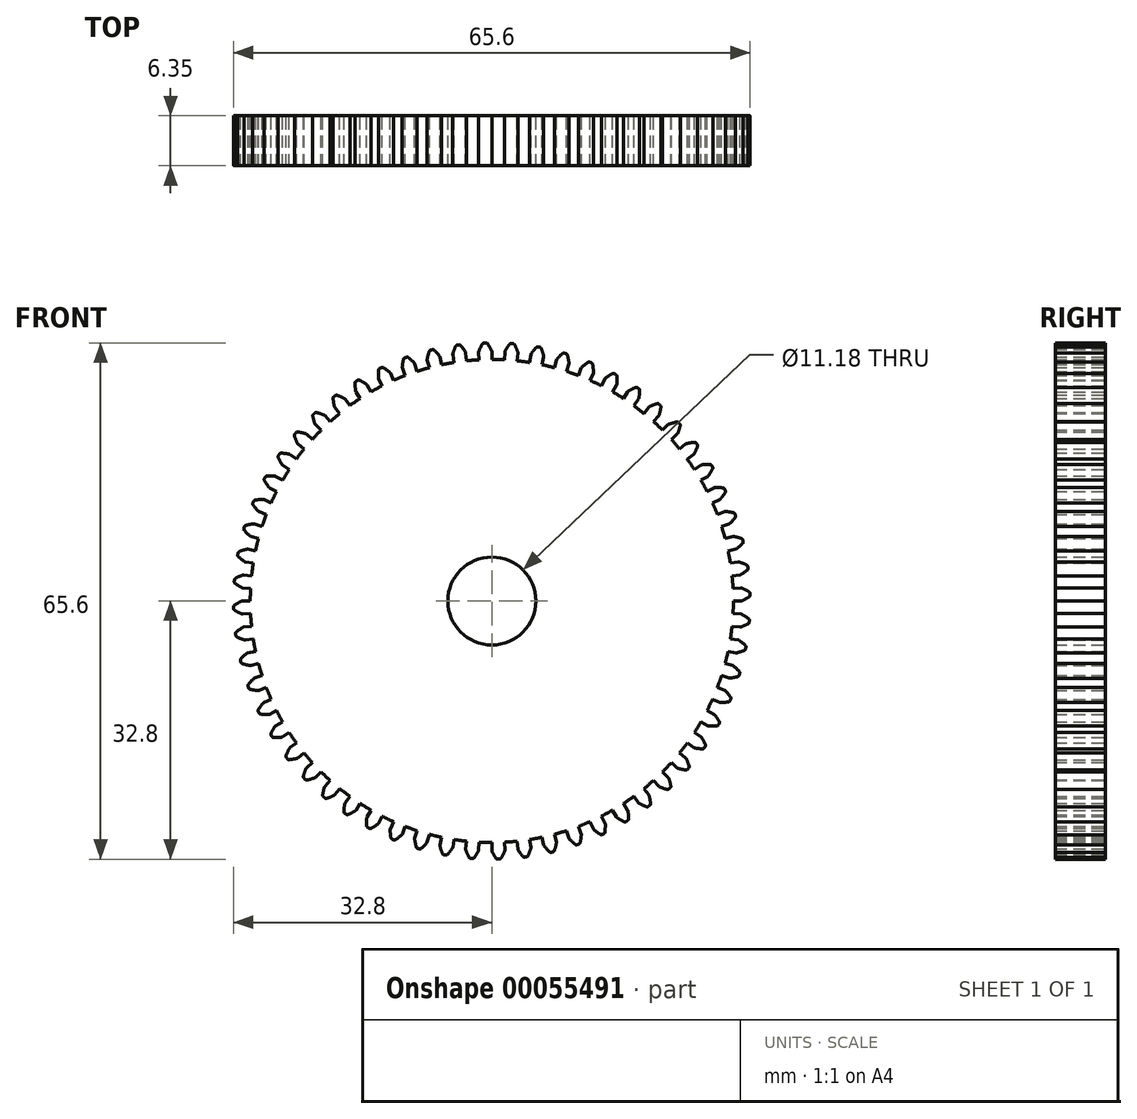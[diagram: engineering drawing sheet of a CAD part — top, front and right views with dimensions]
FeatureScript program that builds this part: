
annotation { "Feature Type Name" : "Feature", "Feature Type Description" : "" }
export const myFeature = defineFeature(function(context is Context, id is Id, definition is map)
    precondition{}
    {
        {
            var Q0;
            Q0=qCreatedBy(makeId("Front.planeOp"),FACE);
            var sketch = newSketch(context, id + "F0", { "sketchPlane" : qUnion([Q0])});
            skCircle(sketch, "E0", {"center": v(0, 0) * mm, "radius": 30.68 * mm});
            skLineSegment(sketch, "E1", {"start": v(0, 0) * mm, "end": v(-0.62, 23.84) * mm, "construction": true});
            skArc(sketch, "E2.trimOffspring", {"start": v(-0.03, 31.8) * mm, "mid": v(-0.26, 32.25) * mm, "end": v(-0.52, 32.68) * mm});
            skLineSegment(sketch, "E3.trimOffspring", {"start": v(-0.62, 23.84) * mm, "end": v(-0.62, 23.84) * mm});
            skArc(sketch, "E4.trimOffspring", {"start": v(-0.74, 32.8) * mm, "mid": v(-0.8, 32.8) * mm, "end": v(-0.86, 32.8) * mm});
            skPoint(sketch, "E5.orphan", {"position": v(-2.53, 48.29) * mm});
            skLineSegment(sketch, "E6", {"start": v(0, 31.7) * mm, "end": v(0, 30.68) * mm});
            skArc(sketch, "E7.MirrorCS", {"start": v(-0.98, 32.79) * mm, "mid": v(-0.92, 32.8) * mm, "end": v(-0.86, 32.8) * mm});
            skArc(sketch, "E8.MirrorCS", {"start": v(-1.64, 31.76) * mm, "mid": v(-1.43, 32.22) * mm, "end": v(-1.19, 32.66) * mm});
            skLineSegment(sketch, "E9.MirrorCS", {"start": v(-1.66, 31.65) * mm, "end": v(-1.6, 30.64) * mm});
            skPoint(sketch, "E10.orphan", {"position": v(-1.26, 48.29) * mm});
            skPoint(sketch, "E11.visualSharp", {"position": v(-1.66, 31.7) * mm});
            skArc(sketch, "E11.filletArc", {"start": v(-1.64, 31.76) * mm, "mid": v(-1.66, 31.7) * mm, "end": v(-1.66, 31.65) * mm});
            skPoint(sketch, "E12.visualSharp", {"position": v(-0.6, 32.8) * mm});
            skArc(sketch, "E12.filletArc", {"start": v(-0.52, 32.68) * mm, "mid": v(-0.62, 32.77) * mm, "end": v(-0.74, 32.8) * mm});
            skPoint(sketch, "E13.visualSharp", {"position": v(-1.12, 32.79) * mm});
            skArc(sketch, "E13.filletArc", {"start": v(-0.98, 32.79) * mm, "mid": v(-1.1, 32.75) * mm, "end": v(-1.19, 32.66) * mm});
            skArc(sketch, "E14.filletArc", {"start": v(0, 31.7) * mm, "mid": v(0, 31.75) * mm, "end": v(-0.03, 31.8) * mm});
            skArc(sketch, "E15.1.0", {"start": v(-4.95, 31.42) * mm, "mid": v(-4.79, 31.9) * mm, "end": v(-4.6, 32.36) * mm});
            skLineSegment(sketch, "E15.1.1", {"start": v(-3.31, 31.52) * mm, "end": v(-3.2, 30.52) * mm});
            skLineSegment(sketch, "E15.1.2", {"start": v(-4.96, 31.3) * mm, "end": v(-4.8, 30.3) * mm});
            skPoint(sketch, "E15.1.3", {"position": v(-4.03, 32.56) * mm});
            skPoint(sketch, "E15.1.4", {"position": v(-3.32, 31.58) * mm});
            skArc(sketch, "E15.1.5", {"start": v(-3.35, 31.63) * mm, "mid": v(-3.63, 32.05) * mm, "end": v(-3.94, 32.45) * mm});
            skPoint(sketch, "E15.1.6", {"position": v(-4.54, 32.49) * mm});
            skPoint(sketch, "E15.1.7", {"position": v(-4.97, 31.36) * mm});
            skArc(sketch, "E15.1.8", {"start": v(-3.94, 32.45) * mm, "mid": v(-4.04, 32.52) * mm, "end": v(-4.17, 32.54) * mm});
            skArc(sketch, "E15.1.9", {"start": v(-4.4, 32.5) * mm, "mid": v(-4.52, 32.46) * mm, "end": v(-4.6, 32.36) * mm});
            skArc(sketch, "E15.1.10", {"start": v(-4.4, 32.5) * mm, "mid": v(-4.34, 32.52) * mm, "end": v(-4.28, 32.52) * mm});
            skArc(sketch, "E15.1.11", {"start": v(-4.17, 32.54) * mm, "mid": v(-4.22, 32.53) * mm, "end": v(-4.28, 32.52) * mm});
            skArc(sketch, "E15.1.12", {"start": v(-4.95, 31.42) * mm, "mid": v(-4.96, 31.36) * mm, "end": v(-4.96, 31.3) * mm});
            skArc(sketch, "E15.1.13", {"start": v(-3.31, 31.52) * mm, "mid": v(-3.33, 31.57) * mm, "end": v(-3.35, 31.63) * mm});
            skArc(sketch, "E15.2.0", {"start": v(-8.2, 30.73) * mm, "mid": v(-8.1, 31.22) * mm, "end": v(-7.95, 31.7) * mm});
            skLineSegment(sketch, "E15.2.1", {"start": v(-6.59, 31) * mm, "end": v(-6.38, 30.01) * mm});
            skLineSegment(sketch, "E15.2.2", {"start": v(-8.2, 30.61) * mm, "end": v(-7.94, 29.64) * mm});
            skPoint(sketch, "E15.2.3", {"position": v(-7.4, 31.96) * mm});
            skPoint(sketch, "E15.2.4", {"position": v(-6.6, 31.06) * mm});
            skArc(sketch, "E15.2.5", {"start": v(-6.64, 31.1) * mm, "mid": v(-6.96, 31.5) * mm, "end": v(-7.3, 31.86) * mm});
            skPoint(sketch, "E15.2.6", {"position": v(-7.9, 31.84) * mm});
            skPoint(sketch, "E15.2.7", {"position": v(-8.22, 30.67) * mm});
            skArc(sketch, "E15.2.8", {"start": v(-7.3, 31.86) * mm, "mid": v(-7.42, 31.92) * mm, "end": v(-7.54, 31.92) * mm});
            skArc(sketch, "E15.2.9", {"start": v(-7.77, 31.87) * mm, "mid": v(-7.88, 31.8) * mm, "end": v(-7.95, 31.7) * mm});
            skArc(sketch, "E15.2.10", {"start": v(-7.77, 31.87) * mm, "mid": v(-7.71, 31.88) * mm, "end": v(-7.66, 31.9) * mm});
            skArc(sketch, "E15.2.11", {"start": v(-7.54, 31.92) * mm, "mid": v(-7.6, 31.91) * mm, "end": v(-7.66, 31.9) * mm});
            skArc(sketch, "E15.2.12", {"start": v(-8.2, 30.73) * mm, "mid": v(-8.21, 30.67) * mm, "end": v(-8.2, 30.61) * mm});
            skArc(sketch, "E15.2.13", {"start": v(-6.59, 31) * mm, "mid": v(-6.6, 31.05) * mm, "end": v(-6.64, 31.1) * mm});
            skArc(sketch, "E15.3.0", {"start": v(-11.37, 29.7) * mm, "mid": v(-11.31, 30.2) * mm, "end": v(-11.22, 30.7) * mm});
            skLineSegment(sketch, "E15.3.1", {"start": v(-9.8, 30.14) * mm, "end": v(-9.48, 29.18) * mm});
            skLineSegment(sketch, "E15.3.2", {"start": v(-11.36, 29.59) * mm, "end": v(-11, 28.65) * mm});
            skPoint(sketch, "E15.3.3", {"position": v(-10.7, 31) * mm});
            skPoint(sketch, "E15.3.4", {"position": v(-9.81, 30.2) * mm});
            skArc(sketch, "E15.3.5", {"start": v(-9.85, 30.24) * mm, "mid": v(-10.21, 30.6) * mm, "end": v(-10.6, 30.92) * mm});
            skPoint(sketch, "E15.3.6", {"position": v(-11.2, 30.84) * mm});
            skPoint(sketch, "E15.3.7", {"position": v(-11.38, 29.64) * mm});
            skArc(sketch, "E15.3.8", {"start": v(-10.6, 30.92) * mm, "mid": v(-10.71, 30.97) * mm, "end": v(-10.84, 30.96) * mm});
            skArc(sketch, "E15.3.9", {"start": v(-11.06, 30.88) * mm, "mid": v(-11.17, 30.81) * mm, "end": v(-11.22, 30.7) * mm});
            skArc(sketch, "E15.3.10", {"start": v(-11.06, 30.88) * mm, "mid": v(-11, 30.9) * mm, "end": v(-10.95, 30.92) * mm});
            skArc(sketch, "E15.3.11", {"start": v(-10.84, 30.96) * mm, "mid": v(-10.9, 30.94) * mm, "end": v(-10.95, 30.92) * mm});
            skArc(sketch, "E15.3.12", {"start": v(-11.37, 29.7) * mm, "mid": v(-11.37, 29.64) * mm, "end": v(-11.36, 29.59) * mm});
            skArc(sketch, "E15.3.13", {"start": v(-9.8, 30.14) * mm, "mid": v(-9.82, 30.2) * mm, "end": v(-9.85, 30.24) * mm});
            skArc(sketch, "E15.4.0", {"start": v(-14.42, 28.35) * mm, "mid": v(-14.4, 28.85) * mm, "end": v(-14.37, 29.36) * mm});
            skLineSegment(sketch, "E15.4.1", {"start": v(-12.9, 28.95) * mm, "end": v(-12.48, 28.03) * mm});
            skLineSegment(sketch, "E15.4.2", {"start": v(-14.39, 28.24) * mm, "end": v(-13.93, 27.34) * mm});
            skPoint(sketch, "E15.4.3", {"position": v(-13.9, 29.72) * mm});
            skPoint(sketch, "E15.4.4", {"position": v(-12.91, 29) * mm});
            skArc(sketch, "E15.4.5", {"start": v(-12.96, 29.04) * mm, "mid": v(-13.36, 29.36) * mm, "end": v(-13.77, 29.64) * mm});
            skPoint(sketch, "E15.4.6", {"position": v(-14.35, 29.5) * mm});
            skPoint(sketch, "E15.4.7", {"position": v(-14.41, 28.29) * mm});
            skArc(sketch, "E15.4.8", {"start": v(-13.77, 29.64) * mm, "mid": v(-13.9, 29.68) * mm, "end": v(-14.02, 29.66) * mm});
            skArc(sketch, "E15.4.9", {"start": v(-14.23, 29.56) * mm, "mid": v(-14.33, 29.48) * mm, "end": v(-14.37, 29.36) * mm});
            skArc(sketch, "E15.4.10", {"start": v(-14.23, 29.56) * mm, "mid": v(-14.18, 29.58) * mm, "end": v(-14.12, 29.6) * mm});
            skArc(sketch, "E15.4.11", {"start": v(-14.02, 29.66) * mm, "mid": v(-14.07, 29.63) * mm, "end": v(-14.12, 29.6) * mm});
            skArc(sketch, "E15.4.12", {"start": v(-14.42, 28.35) * mm, "mid": v(-14.4, 28.3) * mm, "end": v(-14.39, 28.24) * mm});
            skArc(sketch, "E15.4.13", {"start": v(-12.9, 28.95) * mm, "mid": v(-12.92, 29) * mm, "end": v(-12.96, 29.04) * mm});
            skArc(sketch, "E15.5.0", {"start": v(-17.3, 26.69) * mm, "mid": v(-17.35, 27.19) * mm, "end": v(-17.36, 27.7) * mm});
            skLineSegment(sketch, "E15.5.1", {"start": v(-15.85, 27.45) * mm, "end": v(-15.34, 26.57) * mm});
            skLineSegment(sketch, "E15.5.2", {"start": v(-17.26, 26.58) * mm, "end": v(-16.71, 25.73) * mm});
            skPoint(sketch, "E15.5.3", {"position": v(-16.92, 28.1) * mm});
            skPoint(sketch, "E15.5.4", {"position": v(-15.87, 27.5) * mm});
            skArc(sketch, "E15.5.5", {"start": v(-15.92, 27.53) * mm, "mid": v(-16.35, 27.8) * mm, "end": v(-16.8, 28.04) * mm});
            skPoint(sketch, "E15.5.6", {"position": v(-17.36, 27.84) * mm});
            skPoint(sketch, "E15.5.7", {"position": v(-17.3, 26.63) * mm});
            skArc(sketch, "E15.5.8", {"start": v(-16.8, 28.04) * mm, "mid": v(-16.92, 28.07) * mm, "end": v(-17.04, 28.03) * mm});
            skArc(sketch, "E15.5.9", {"start": v(-17.24, 27.9) * mm, "mid": v(-17.33, 27.82) * mm, "end": v(-17.36, 27.7) * mm});
            skArc(sketch, "E15.5.10", {"start": v(-17.24, 27.9) * mm, "mid": v(-17.19, 27.94) * mm, "end": v(-17.14, 27.97) * mm});
            skArc(sketch, "E15.5.11", {"start": v(-17.04, 28.03) * mm, "mid": v(-17.1, 28) * mm, "end": v(-17.14, 27.97) * mm});
            skArc(sketch, "E15.5.12", {"start": v(-17.3, 26.69) * mm, "mid": v(-17.29, 26.63) * mm, "end": v(-17.26, 26.58) * mm});
            skArc(sketch, "E15.5.13", {"start": v(-15.85, 27.45) * mm, "mid": v(-15.88, 27.5) * mm, "end": v(-15.92, 27.53) * mm});
            skArc(sketch, "E15.6.0", {"start": v(-20, 24.73) * mm, "mid": v(-20.1, 25.23) * mm, "end": v(-20.16, 25.73) * mm});
            skLineSegment(sketch, "E15.6.1", {"start": v(-18.63, 25.64) * mm, "end": v(-18.04, 24.82) * mm});
            skLineSegment(sketch, "E15.6.2", {"start": v(-19.94, 24.63) * mm, "end": v(-19.3, 23.85) * mm});
            skPoint(sketch, "E15.6.3", {"position": v(-19.77, 26.18) * mm});
            skPoint(sketch, "E15.6.4", {"position": v(-18.66, 25.69) * mm});
            skArc(sketch, "E15.6.5", {"start": v(-18.71, 25.71) * mm, "mid": v(-19.17, 25.94) * mm, "end": v(-19.63, 26.13) * mm});
            skPoint(sketch, "E15.6.6", {"position": v(-20.17, 25.87) * mm});
            skPoint(sketch, "E15.6.7", {"position": v(-19.98, 24.67) * mm});
            skArc(sketch, "E15.6.8", {"start": v(-19.63, 26.13) * mm, "mid": v(-19.76, 26.15) * mm, "end": v(-19.88, 26.1) * mm});
            skArc(sketch, "E15.6.9", {"start": v(-20.06, 25.95) * mm, "mid": v(-20.14, 25.85) * mm, "end": v(-20.16, 25.73) * mm});
            skArc(sketch, "E15.6.10", {"start": v(-20.06, 25.95) * mm, "mid": v(-20.02, 25.99) * mm, "end": v(-19.97, 26.03) * mm});
            skArc(sketch, "E15.6.11", {"start": v(-19.88, 26.1) * mm, "mid": v(-19.92, 26.06) * mm, "end": v(-19.97, 26.03) * mm});
            skArc(sketch, "E15.6.12", {"start": v(-20, 24.73) * mm, "mid": v(-19.98, 24.68) * mm, "end": v(-19.94, 24.63) * mm});
            skArc(sketch, "E15.6.13", {"start": v(-18.63, 25.64) * mm, "mid": v(-18.67, 25.68) * mm, "end": v(-18.71, 25.71) * mm});
            skArc(sketch, "E15.7.0", {"start": v(-22.47, 22.5) * mm, "mid": v(-22.62, 22.99) * mm, "end": v(-22.74, 23.48) * mm});
            skLineSegment(sketch, "E15.7.1", {"start": v(-21.2, 23.55) * mm, "end": v(-20.53, 22.8) * mm});
            skLineSegment(sketch, "E15.7.2", {"start": v(-22.4, 22.4) * mm, "end": v(-21.7, 21.7) * mm});
            skPoint(sketch, "E15.7.3", {"position": v(-22.4, 23.97) * mm});
            skPoint(sketch, "E15.7.4", {"position": v(-21.24, 23.6) * mm});
            skArc(sketch, "E15.7.5", {"start": v(-21.3, 23.62) * mm, "mid": v(-21.77, 23.8) * mm, "end": v(-22.26, 23.94) * mm});
            skPoint(sketch, "E15.7.6", {"position": v(-22.77, 23.62) * mm});
            skPoint(sketch, "E15.7.7", {"position": v(-22.45, 22.45) * mm});
            skArc(sketch, "E15.7.8", {"start": v(-22.26, 23.94) * mm, "mid": v(-22.38, 23.94) * mm, "end": v(-22.5, 23.88) * mm});
            skArc(sketch, "E15.7.9", {"start": v(-22.67, 23.71) * mm, "mid": v(-22.73, 23.6) * mm, "end": v(-22.74, 23.48) * mm});
            skArc(sketch, "E15.7.10", {"start": v(-22.67, 23.71) * mm, "mid": v(-22.62, 23.75) * mm, "end": v(-22.58, 23.8) * mm});
            skArc(sketch, "E15.7.11", {"start": v(-22.5, 23.88) * mm, "mid": v(-22.54, 23.84) * mm, "end": v(-22.58, 23.8) * mm});
            skArc(sketch, "E15.7.12", {"start": v(-22.47, 22.5) * mm, "mid": v(-22.45, 22.45) * mm, "end": v(-22.4, 22.4) * mm});
            skArc(sketch, "E15.7.13", {"start": v(-21.2, 23.55) * mm, "mid": v(-21.25, 23.59) * mm, "end": v(-21.3, 23.62) * mm});
            skArc(sketch, "E15.8.0", {"start": v(-24.7, 20.03) * mm, "mid": v(-24.9, 20.5) * mm, "end": v(-25.07, 20.97) * mm});
            skLineSegment(sketch, "E15.8.1", {"start": v(-23.55, 21.2) * mm, "end": v(-22.8, 20.53) * mm});
            skLineSegment(sketch, "E15.8.2", {"start": v(-24.63, 19.94) * mm, "end": v(-23.85, 19.3) * mm});
            skPoint(sketch, "E15.8.3", {"position": v(-24.78, 21.5) * mm});
            skPoint(sketch, "E15.8.4", {"position": v(-23.6, 21.24) * mm});
            skArc(sketch, "E15.8.5", {"start": v(-23.65, 21.26) * mm, "mid": v(-24.14, 21.39) * mm, "end": v(-24.64, 21.48) * mm});
            skPoint(sketch, "E15.8.6", {"position": v(-25.11, 21.1) * mm});
            skPoint(sketch, "E15.8.7", {"position": v(-24.67, 19.98) * mm});
            skArc(sketch, "E15.8.8", {"start": v(-24.64, 21.48) * mm, "mid": v(-24.76, 21.47) * mm, "end": v(-24.87, 21.4) * mm});
            skArc(sketch, "E15.8.9", {"start": v(-25.02, 21.22) * mm, "mid": v(-25.08, 21.1) * mm, "end": v(-25.07, 20.97) * mm});
            skArc(sketch, "E15.8.10", {"start": v(-25.02, 21.22) * mm, "mid": v(-24.98, 21.26) * mm, "end": v(-24.94, 21.3) * mm});
            skArc(sketch, "E15.8.11", {"start": v(-24.87, 21.4) * mm, "mid": v(-24.9, 21.35) * mm, "end": v(-24.94, 21.3) * mm});
            skArc(sketch, "E15.8.12", {"start": v(-24.7, 20.03) * mm, "mid": v(-24.67, 19.99) * mm, "end": v(-24.63, 19.94) * mm});
            skArc(sketch, "E15.8.13", {"start": v(-23.55, 21.2) * mm, "mid": v(-23.6, 21.24) * mm, "end": v(-23.65, 21.26) * mm});
            skArc(sketch, "E15.9.0", {"start": v(-26.66, 17.34) * mm, "mid": v(-26.9, 17.78) * mm, "end": v(-27.12, 18.24) * mm});
            skLineSegment(sketch, "E15.9.1", {"start": v(-25.64, 18.63) * mm, "end": v(-24.82, 18.04) * mm});
            skLineSegment(sketch, "E15.9.2", {"start": v(-26.58, 17.26) * mm, "end": v(-25.73, 16.71) * mm});
            skPoint(sketch, "E15.9.3", {"position": v(-26.89, 18.8) * mm});
            skPoint(sketch, "E15.9.4", {"position": v(-25.69, 18.66) * mm});
            skArc(sketch, "E15.9.5", {"start": v(-25.74, 18.67) * mm, "mid": v(-26.24, 18.75) * mm, "end": v(-26.75, 18.79) * mm});
            skPoint(sketch, "E15.9.6", {"position": v(-27.18, 18.37) * mm});
            skPoint(sketch, "E15.9.7", {"position": v(-26.63, 17.3) * mm});
            skArc(sketch, "E15.9.8", {"start": v(-26.75, 18.79) * mm, "mid": v(-26.87, 18.76) * mm, "end": v(-26.97, 18.68) * mm});
            skArc(sketch, "E15.9.9", {"start": v(-27.1, 18.48) * mm, "mid": v(-27.14, 18.36) * mm, "end": v(-27.12, 18.24) * mm});
            skArc(sketch, "E15.9.10", {"start": v(-27.1, 18.48) * mm, "mid": v(-27.07, 18.53) * mm, "end": v(-27.03, 18.58) * mm});
            skArc(sketch, "E15.9.11", {"start": v(-26.97, 18.68) * mm, "mid": v(-27, 18.63) * mm, "end": v(-27.03, 18.58) * mm});
            skArc(sketch, "E15.9.12", {"start": v(-26.66, 17.34) * mm, "mid": v(-26.62, 17.3) * mm, "end": v(-26.58, 17.26) * mm});
            skArc(sketch, "E15.9.13", {"start": v(-25.64, 18.63) * mm, "mid": v(-25.69, 18.66) * mm, "end": v(-25.74, 18.67) * mm});
            skArc(sketch, "E15.10.0", {"start": v(-28.33, 14.46) * mm, "mid": v(-28.62, 14.87) * mm, "end": v(-28.88, 15.3) * mm});
            skLineSegment(sketch, "E15.10.1", {"start": v(-27.45, 15.85) * mm, "end": v(-26.57, 15.34) * mm});
            skLineSegment(sketch, "E15.10.2", {"start": v(-28.24, 14.39) * mm, "end": v(-27.34, 13.93) * mm});
            skPoint(sketch, "E15.10.3", {"position": v(-28.7, 15.88) * mm});
            skPoint(sketch, "E15.10.4", {"position": v(-27.5, 15.88) * mm});
            skArc(sketch, "E15.10.5", {"start": v(-27.56, 15.88) * mm, "mid": v(-28.06, 15.9) * mm, "end": v(-28.56, 15.89) * mm});
            skPoint(sketch, "E15.10.6", {"position": v(-28.95, 15.43) * mm});
            skPoint(sketch, "E15.10.7", {"position": v(-28.29, 14.41) * mm});
            skArc(sketch, "E15.10.8", {"start": v(-28.56, 15.89) * mm, "mid": v(-28.69, 15.85) * mm, "end": v(-28.77, 15.76) * mm});
            skArc(sketch, "E15.10.9", {"start": v(-28.88, 15.55) * mm, "mid": v(-28.91, 15.43) * mm, "end": v(-28.88, 15.3) * mm});
            skArc(sketch, "E15.10.10", {"start": v(-28.88, 15.55) * mm, "mid": v(-28.86, 15.6) * mm, "end": v(-28.83, 15.65) * mm});
            skArc(sketch, "E15.10.11", {"start": v(-28.77, 15.76) * mm, "mid": v(-28.8, 15.7) * mm, "end": v(-28.83, 15.65) * mm});
            skArc(sketch, "E15.10.12", {"start": v(-28.33, 14.46) * mm, "mid": v(-28.29, 14.42) * mm, "end": v(-28.24, 14.39) * mm});
            skArc(sketch, "E15.10.13", {"start": v(-27.45, 15.85) * mm, "mid": v(-27.5, 15.87) * mm, "end": v(-27.56, 15.88) * mm});
            skArc(sketch, "E15.11.0", {"start": v(-29.68, 11.42) * mm, "mid": v(-30.01, 11.8) * mm, "end": v(-30.32, 12.2) * mm});
            skLineSegment(sketch, "E15.11.1", {"start": v(-28.95, 12.9) * mm, "end": v(-28.03, 12.48) * mm});
            skLineSegment(sketch, "E15.11.2", {"start": v(-29.59, 11.36) * mm, "end": v(-28.65, 11) * mm});
            skPoint(sketch, "E15.11.3", {"position": v(-30.2, 12.8) * mm});
            skPoint(sketch, "E15.11.4", {"position": v(-29, 12.91) * mm});
            skArc(sketch, "E15.11.5", {"start": v(-29.06, 12.91) * mm, "mid": v(-29.57, 12.88) * mm, "end": v(-30.07, 12.81) * mm});
            skPoint(sketch, "E15.11.6", {"position": v(-30.4, 12.32) * mm});
            skPoint(sketch, "E15.11.7", {"position": v(-29.64, 11.38) * mm});
            skArc(sketch, "E15.11.8", {"start": v(-30.07, 12.81) * mm, "mid": v(-30.18, 12.76) * mm, "end": v(-30.26, 12.66) * mm});
            skArc(sketch, "E15.11.9", {"start": v(-30.35, 12.45) * mm, "mid": v(-30.37, 12.32) * mm, "end": v(-30.32, 12.2) * mm});
            skArc(sketch, "E15.11.10", {"start": v(-30.35, 12.45) * mm, "mid": v(-30.33, 12.5) * mm, "end": v(-30.3, 12.55) * mm});
            skArc(sketch, "E15.11.11", {"start": v(-30.26, 12.66) * mm, "mid": v(-30.28, 12.6) * mm, "end": v(-30.3, 12.55) * mm});
            skArc(sketch, "E15.11.12", {"start": v(-29.68, 11.42) * mm, "mid": v(-29.64, 11.38) * mm, "end": v(-29.59, 11.36) * mm});
            skArc(sketch, "E15.11.13", {"start": v(-28.95, 12.9) * mm, "mid": v(-29, 12.9) * mm, "end": v(-29.06, 12.91) * mm});
            skArc(sketch, "E15.12.0", {"start": v(-30.71, 8.26) * mm, "mid": v(-31.08, 8.6) * mm, "end": v(-31.43, 8.96) * mm});
            skLineSegment(sketch, "E15.12.1", {"start": v(-30.14, 9.8) * mm, "end": v(-29.18, 9.48) * mm});
            skLineSegment(sketch, "E15.12.2", {"start": v(-30.61, 8.2) * mm, "end": v(-29.64, 7.94) * mm});
            skPoint(sketch, "E15.12.3", {"position": v(-31.38, 9.56) * mm});
            skPoint(sketch, "E15.12.4", {"position": v(-30.2, 9.81) * mm});
            skArc(sketch, "E15.12.5", {"start": v(-30.25, 9.8) * mm, "mid": v(-30.75, 9.72) * mm, "end": v(-31.24, 9.6) * mm});
            skPoint(sketch, "E15.12.6", {"position": v(-31.53, 9.07) * mm});
            skPoint(sketch, "E15.12.7", {"position": v(-30.67, 8.22) * mm});
            skArc(sketch, "E15.12.8", {"start": v(-31.24, 9.6) * mm, "mid": v(-31.35, 9.54) * mm, "end": v(-31.42, 9.43) * mm});
            skArc(sketch, "E15.12.9", {"start": v(-31.49, 9.2) * mm, "mid": v(-31.5, 9.08) * mm, "end": v(-31.43, 8.96) * mm});
            skArc(sketch, "E15.12.10", {"start": v(-31.49, 9.2) * mm, "mid": v(-31.47, 9.26) * mm, "end": v(-31.45, 9.32) * mm});
            skArc(sketch, "E15.12.11", {"start": v(-31.42, 9.43) * mm, "mid": v(-31.44, 9.37) * mm, "end": v(-31.45, 9.32) * mm});
            skArc(sketch, "E15.12.12", {"start": v(-30.71, 8.26) * mm, "mid": v(-30.67, 8.22) * mm, "end": v(-30.61, 8.2) * mm});
            skArc(sketch, "E15.12.13", {"start": v(-30.14, 9.8) * mm, "mid": v(-30.2, 9.8) * mm, "end": v(-30.25, 9.8) * mm});
            skArc(sketch, "E15.13.0", {"start": v(-31.4, 5) * mm, "mid": v(-31.81, 5.3) * mm, "end": v(-32.2, 5.63) * mm});
            skLineSegment(sketch, "E15.13.1", {"start": v(-31, 6.59) * mm, "end": v(-30.01, 6.38) * mm});
            skLineSegment(sketch, "E15.13.2", {"start": v(-31.3, 4.96) * mm, "end": v(-30.3, 4.8) * mm});
            skPoint(sketch, "E15.13.3", {"position": v(-32.2, 6.23) * mm});
            skPoint(sketch, "E15.13.4", {"position": v(-31.06, 6.6) * mm});
            skArc(sketch, "E15.13.5", {"start": v(-31.11, 6.59) * mm, "mid": v(-31.6, 6.45) * mm, "end": v(-32.08, 6.28) * mm});
            skPoint(sketch, "E15.13.6", {"position": v(-32.3, 5.73) * mm});
            skPoint(sketch, "E15.13.7", {"position": v(-31.36, 4.97) * mm});
            skArc(sketch, "E15.13.8", {"start": v(-32.08, 6.28) * mm, "mid": v(-32.18, 6.2) * mm, "end": v(-32.23, 6.1) * mm});
            skArc(sketch, "E15.13.9", {"start": v(-32.28, 5.86) * mm, "mid": v(-32.27, 5.74) * mm, "end": v(-32.2, 5.63) * mm});
            skArc(sketch, "E15.13.10", {"start": v(-32.28, 5.86) * mm, "mid": v(-32.27, 5.92) * mm, "end": v(-32.25, 5.98) * mm});
            skArc(sketch, "E15.13.11", {"start": v(-32.23, 6.1) * mm, "mid": v(-32.24, 6.04) * mm, "end": v(-32.25, 5.98) * mm});
            skArc(sketch, "E15.13.12", {"start": v(-31.4, 5) * mm, "mid": v(-31.36, 4.97) * mm, "end": v(-31.3, 4.96) * mm});
            skArc(sketch, "E15.13.13", {"start": v(-31, 6.59) * mm, "mid": v(-31.06, 6.6) * mm, "end": v(-31.11, 6.59) * mm});
            skArc(sketch, "E15.14.0", {"start": v(-31.76, 1.69) * mm, "mid": v(-32.2, 1.95) * mm, "end": v(-32.6, 2.23) * mm});
            skLineSegment(sketch, "E15.14.1", {"start": v(-31.52, 3.31) * mm, "end": v(-30.52, 3.2) * mm});
            skLineSegment(sketch, "E15.14.2", {"start": v(-31.65, 1.66) * mm, "end": v(-30.64, 1.6) * mm});
            skPoint(sketch, "E15.14.3", {"position": v(-32.68, 2.83) * mm});
            skPoint(sketch, "E15.14.4", {"position": v(-31.58, 3.32) * mm});
            skArc(sketch, "E15.14.5", {"start": v(-31.63, 3.3) * mm, "mid": v(-32.1, 3.11) * mm, "end": v(-32.56, 2.9) * mm});
            skPoint(sketch, "E15.14.6", {"position": v(-32.72, 2.32) * mm});
            skPoint(sketch, "E15.14.7", {"position": v(-31.7, 1.66) * mm});
            skArc(sketch, "E15.14.8", {"start": v(-32.56, 2.9) * mm, "mid": v(-32.65, 2.81) * mm, "end": v(-32.7, 2.7) * mm});
            skArc(sketch, "E15.14.9", {"start": v(-32.71, 2.46) * mm, "mid": v(-32.69, 2.33) * mm, "end": v(-32.6, 2.23) * mm});
            skArc(sketch, "E15.14.10", {"start": v(-32.71, 2.46) * mm, "mid": v(-32.7, 2.52) * mm, "end": v(-32.7, 2.57) * mm});
            skArc(sketch, "E15.14.11", {"start": v(-32.7, 2.7) * mm, "mid": v(-32.7, 2.63) * mm, "end": v(-32.7, 2.57) * mm});
            skArc(sketch, "E15.14.12", {"start": v(-31.76, 1.69) * mm, "mid": v(-31.7, 1.67) * mm, "end": v(-31.65, 1.66) * mm});
            skArc(sketch, "E15.14.13", {"start": v(-31.52, 3.31) * mm, "mid": v(-31.58, 3.31) * mm, "end": v(-31.63, 3.3) * mm});
            skArc(sketch, "E15.15.0", {"start": v(-31.76, -1.64) * mm, "mid": v(-32.22, -1.43) * mm, "end": v(-32.66, -1.19) * mm});
            skLineSegment(sketch, "E15.15.1", {"start": v(-31.7, 0) * mm, "end": v(-30.68, 0) * mm});
            skLineSegment(sketch, "E15.15.2", {"start": v(-31.65, -1.66) * mm, "end": v(-30.64, -1.6) * mm});
            skPoint(sketch, "E15.15.3", {"position": v(-32.8, -0.6) * mm});
            skPoint(sketch, "E15.15.4", {"position": v(-31.75, 0) * mm});
            skArc(sketch, "E15.15.5", {"start": v(-31.8, -0.03) * mm, "mid": v(-32.25, -0.26) * mm, "end": v(-32.68, -0.52) * mm});
            skPoint(sketch, "E15.15.6", {"position": v(-32.79, -1.12) * mm});
            skPoint(sketch, "E15.15.7", {"position": v(-31.7, -1.66) * mm});
            skArc(sketch, "E15.15.8", {"start": v(-32.68, -0.52) * mm, "mid": v(-32.77, -0.62) * mm, "end": v(-32.8, -0.74) * mm});
            skArc(sketch, "E15.15.9", {"start": v(-32.79, -0.98) * mm, "mid": v(-32.75, -1.1) * mm, "end": v(-32.66, -1.19) * mm});
            skArc(sketch, "E15.15.10", {"start": v(-32.79, -0.98) * mm, "mid": v(-32.8, -0.92) * mm, "end": v(-32.8, -0.86) * mm});
            skArc(sketch, "E15.15.11", {"start": v(-32.8, -0.74) * mm, "mid": v(-32.8, -0.8) * mm, "end": v(-32.8, -0.86) * mm});
            skArc(sketch, "E15.15.12", {"start": v(-31.76, -1.64) * mm, "mid": v(-31.7, -1.66) * mm, "end": v(-31.65, -1.66) * mm});
            skArc(sketch, "E15.15.13", {"start": v(-31.7, 0) * mm, "mid": v(-31.75, 0) * mm, "end": v(-31.8, -0.03) * mm});
            skArc(sketch, "E15.16.0", {"start": v(-31.42, -4.95) * mm, "mid": v(-31.9, -4.79) * mm, "end": v(-32.36, -4.6) * mm});
            skLineSegment(sketch, "E15.16.1", {"start": v(-31.52, -3.31) * mm, "end": v(-30.52, -3.2) * mm});
            skLineSegment(sketch, "E15.16.2", {"start": v(-31.3, -4.96) * mm, "end": v(-30.3, -4.8) * mm});
            skPoint(sketch, "E15.16.3", {"position": v(-32.56, -4.03) * mm});
            skPoint(sketch, "E15.16.4", {"position": v(-31.58, -3.32) * mm});
            skArc(sketch, "E15.16.5", {"start": v(-31.63, -3.35) * mm, "mid": v(-32.05, -3.63) * mm, "end": v(-32.45, -3.94) * mm});
            skPoint(sketch, "E15.16.6", {"position": v(-32.49, -4.54) * mm});
            skPoint(sketch, "E15.16.7", {"position": v(-31.36, -4.97) * mm});
            skArc(sketch, "E15.16.8", {"start": v(-32.45, -3.94) * mm, "mid": v(-32.52, -4.04) * mm, "end": v(-32.54, -4.17) * mm});
            skArc(sketch, "E15.16.9", {"start": v(-32.5, -4.4) * mm, "mid": v(-32.46, -4.52) * mm, "end": v(-32.36, -4.6) * mm});
            skArc(sketch, "E15.16.10", {"start": v(-32.5, -4.4) * mm, "mid": v(-32.52, -4.34) * mm, "end": v(-32.52, -4.28) * mm});
            skArc(sketch, "E15.16.11", {"start": v(-32.54, -4.17) * mm, "mid": v(-32.53, -4.22) * mm, "end": v(-32.52, -4.28) * mm});
            skArc(sketch, "E15.16.12", {"start": v(-31.42, -4.95) * mm, "mid": v(-31.36, -4.96) * mm, "end": v(-31.3, -4.96) * mm});
            skArc(sketch, "E15.16.13", {"start": v(-31.52, -3.31) * mm, "mid": v(-31.57, -3.33) * mm, "end": v(-31.63, -3.35) * mm});
            skArc(sketch, "E15.17.0", {"start": v(-30.73, -8.2) * mm, "mid": v(-31.22, -8.1) * mm, "end": v(-31.7, -7.95) * mm});
            skLineSegment(sketch, "E15.17.1", {"start": v(-31, -6.59) * mm, "end": v(-30.01, -6.38) * mm});
            skLineSegment(sketch, "E15.17.2", {"start": v(-30.61, -8.2) * mm, "end": v(-29.64, -7.94) * mm});
            skPoint(sketch, "E15.17.3", {"position": v(-31.96, -7.4) * mm});
            skPoint(sketch, "E15.17.4", {"position": v(-31.06, -6.6) * mm});
            skArc(sketch, "E15.17.5", {"start": v(-31.1, -6.64) * mm, "mid": v(-31.5, -6.96) * mm, "end": v(-31.86, -7.3) * mm});
            skPoint(sketch, "E15.17.6", {"position": v(-31.84, -7.9) * mm});
            skPoint(sketch, "E15.17.7", {"position": v(-30.67, -8.22) * mm});
            skArc(sketch, "E15.17.8", {"start": v(-31.86, -7.3) * mm, "mid": v(-31.92, -7.42) * mm, "end": v(-31.92, -7.54) * mm});
            skArc(sketch, "E15.17.9", {"start": v(-31.87, -7.77) * mm, "mid": v(-31.8, -7.88) * mm, "end": v(-31.7, -7.95) * mm});
            skArc(sketch, "E15.17.10", {"start": v(-31.87, -7.77) * mm, "mid": v(-31.88, -7.71) * mm, "end": v(-31.9, -7.66) * mm});
            skArc(sketch, "E15.17.11", {"start": v(-31.92, -7.54) * mm, "mid": v(-31.91, -7.6) * mm, "end": v(-31.9, -7.66) * mm});
            skArc(sketch, "E15.17.12", {"start": v(-30.73, -8.2) * mm, "mid": v(-30.67, -8.21) * mm, "end": v(-30.61, -8.2) * mm});
            skArc(sketch, "E15.17.13", {"start": v(-31, -6.59) * mm, "mid": v(-31.05, -6.6) * mm, "end": v(-31.1, -6.64) * mm});
            skArc(sketch, "E15.18.0", {"start": v(-29.7, -11.37) * mm, "mid": v(-30.2, -11.31) * mm, "end": v(-30.7, -11.22) * mm});
            skLineSegment(sketch, "E15.18.1", {"start": v(-30.14, -9.8) * mm, "end": v(-29.18, -9.48) * mm});
            skLineSegment(sketch, "E15.18.2", {"start": v(-29.59, -11.36) * mm, "end": v(-28.65, -11) * mm});
            skPoint(sketch, "E15.18.3", {"position": v(-31, -10.7) * mm});
            skPoint(sketch, "E15.18.4", {"position": v(-30.2, -9.81) * mm});
            skArc(sketch, "E15.18.5", {"start": v(-30.24, -9.85) * mm, "mid": v(-30.6, -10.21) * mm, "end": v(-30.92, -10.6) * mm});
            skPoint(sketch, "E15.18.6", {"position": v(-30.84, -11.2) * mm});
            skPoint(sketch, "E15.18.7", {"position": v(-29.64, -11.38) * mm});
            skArc(sketch, "E15.18.8", {"start": v(-30.92, -10.6) * mm, "mid": v(-30.97, -10.71) * mm, "end": v(-30.96, -10.84) * mm});
            skArc(sketch, "E15.18.9", {"start": v(-30.88, -11.06) * mm, "mid": v(-30.81, -11.17) * mm, "end": v(-30.7, -11.22) * mm});
            skArc(sketch, "E15.18.10", {"start": v(-30.88, -11.06) * mm, "mid": v(-30.9, -11) * mm, "end": v(-30.92, -10.95) * mm});
            skArc(sketch, "E15.18.11", {"start": v(-30.96, -10.84) * mm, "mid": v(-30.94, -10.9) * mm, "end": v(-30.92, -10.95) * mm});
            skArc(sketch, "E15.18.12", {"start": v(-29.7, -11.37) * mm, "mid": v(-29.64, -11.37) * mm, "end": v(-29.59, -11.36) * mm});
            skArc(sketch, "E15.18.13", {"start": v(-30.14, -9.8) * mm, "mid": v(-30.2, -9.82) * mm, "end": v(-30.24, -9.85) * mm});
            skArc(sketch, "E15.19.0", {"start": v(-28.35, -14.42) * mm, "mid": v(-28.85, -14.4) * mm, "end": v(-29.36, -14.37) * mm});
            skLineSegment(sketch, "E15.19.1", {"start": v(-28.95, -12.9) * mm, "end": v(-28.03, -12.48) * mm});
            skLineSegment(sketch, "E15.19.2", {"start": v(-28.24, -14.39) * mm, "end": v(-27.34, -13.93) * mm});
            skPoint(sketch, "E15.19.3", {"position": v(-29.72, -13.9) * mm});
            skPoint(sketch, "E15.19.4", {"position": v(-29, -12.91) * mm});
            skArc(sketch, "E15.19.5", {"start": v(-29.04, -12.96) * mm, "mid": v(-29.36, -13.36) * mm, "end": v(-29.64, -13.77) * mm});
            skPoint(sketch, "E15.19.6", {"position": v(-29.5, -14.35) * mm});
            skPoint(sketch, "E15.19.7", {"position": v(-28.29, -14.41) * mm});
            skArc(sketch, "E15.19.8", {"start": v(-29.64, -13.77) * mm, "mid": v(-29.68, -13.9) * mm, "end": v(-29.66, -14.02) * mm});
            skArc(sketch, "E15.19.9", {"start": v(-29.56, -14.23) * mm, "mid": v(-29.48, -14.33) * mm, "end": v(-29.36, -14.37) * mm});
            skArc(sketch, "E15.19.10", {"start": v(-29.56, -14.23) * mm, "mid": v(-29.58, -14.18) * mm, "end": v(-29.6, -14.12) * mm});
            skArc(sketch, "E15.19.11", {"start": v(-29.66, -14.02) * mm, "mid": v(-29.63, -14.07) * mm, "end": v(-29.6, -14.12) * mm});
            skArc(sketch, "E15.19.12", {"start": v(-28.35, -14.42) * mm, "mid": v(-28.3, -14.4) * mm, "end": v(-28.24, -14.39) * mm});
            skArc(sketch, "E15.19.13", {"start": v(-28.95, -12.9) * mm, "mid": v(-29, -12.92) * mm, "end": v(-29.04, -12.96) * mm});
            skArc(sketch, "E15.20.0", {"start": v(-26.69, -17.3) * mm, "mid": v(-27.19, -17.35) * mm, "end": v(-27.7, -17.36) * mm});
            skLineSegment(sketch, "E15.20.1", {"start": v(-27.45, -15.85) * mm, "end": v(-26.57, -15.34) * mm});
            skLineSegment(sketch, "E15.20.2", {"start": v(-26.58, -17.26) * mm, "end": v(-25.73, -16.71) * mm});
            skPoint(sketch, "E15.20.3", {"position": v(-28.1, -16.92) * mm});
            skPoint(sketch, "E15.20.4", {"position": v(-27.5, -15.87) * mm});
            skArc(sketch, "E15.20.5", {"start": v(-27.53, -15.92) * mm, "mid": v(-27.8, -16.35) * mm, "end": v(-28.04, -16.8) * mm});
            skPoint(sketch, "E15.20.6", {"position": v(-27.84, -17.36) * mm});
            skPoint(sketch, "E15.20.7", {"position": v(-26.63, -17.3) * mm});
            skArc(sketch, "E15.20.8", {"start": v(-28.04, -16.8) * mm, "mid": v(-28.07, -16.92) * mm, "end": v(-28.03, -17.04) * mm});
            skArc(sketch, "E15.20.9", {"start": v(-27.9, -17.24) * mm, "mid": v(-27.82, -17.33) * mm, "end": v(-27.7, -17.36) * mm});
            skArc(sketch, "E15.20.10", {"start": v(-27.9, -17.24) * mm, "mid": v(-27.94, -17.19) * mm, "end": v(-27.97, -17.14) * mm});
            skArc(sketch, "E15.20.11", {"start": v(-28.03, -17.04) * mm, "mid": v(-28, -17.1) * mm, "end": v(-27.97, -17.14) * mm});
            skArc(sketch, "E15.20.12", {"start": v(-26.69, -17.3) * mm, "mid": v(-26.63, -17.29) * mm, "end": v(-26.58, -17.26) * mm});
            skArc(sketch, "E15.20.13", {"start": v(-27.45, -15.85) * mm, "mid": v(-27.5, -15.88) * mm, "end": v(-27.53, -15.92) * mm});
            skArc(sketch, "E15.21.0", {"start": v(-24.73, -20) * mm, "mid": v(-25.23, -20.1) * mm, "end": v(-25.73, -20.16) * mm});
            skLineSegment(sketch, "E15.21.1", {"start": v(-25.64, -18.63) * mm, "end": v(-24.82, -18.04) * mm});
            skLineSegment(sketch, "E15.21.2", {"start": v(-24.63, -19.94) * mm, "end": v(-23.85, -19.3) * mm});
            skPoint(sketch, "E15.21.3", {"position": v(-26.18, -19.77) * mm});
            skPoint(sketch, "E15.21.4", {"position": v(-25.69, -18.66) * mm});
            skArc(sketch, "E15.21.5", {"start": v(-25.71, -18.71) * mm, "mid": v(-25.94, -19.17) * mm, "end": v(-26.13, -19.63) * mm});
            skPoint(sketch, "E15.21.6", {"position": v(-25.87, -20.17) * mm});
            skPoint(sketch, "E15.21.7", {"position": v(-24.67, -19.98) * mm});
            skArc(sketch, "E15.21.8", {"start": v(-26.13, -19.63) * mm, "mid": v(-26.15, -19.76) * mm, "end": v(-26.1, -19.88) * mm});
            skArc(sketch, "E15.21.9", {"start": v(-25.95, -20.06) * mm, "mid": v(-25.85, -20.14) * mm, "end": v(-25.73, -20.16) * mm});
            skArc(sketch, "E15.21.10", {"start": v(-25.95, -20.06) * mm, "mid": v(-25.99, -20.02) * mm, "end": v(-26.03, -19.97) * mm});
            skArc(sketch, "E15.21.11", {"start": v(-26.1, -19.88) * mm, "mid": v(-26.06, -19.92) * mm, "end": v(-26.03, -19.97) * mm});
            skArc(sketch, "E15.21.12", {"start": v(-24.73, -20) * mm, "mid": v(-24.68, -19.98) * mm, "end": v(-24.63, -19.94) * mm});
            skArc(sketch, "E15.21.13", {"start": v(-25.64, -18.63) * mm, "mid": v(-25.68, -18.67) * mm, "end": v(-25.71, -18.71) * mm});
            skArc(sketch, "E15.22.0", {"start": v(-22.5, -22.47) * mm, "mid": v(-22.99, -22.62) * mm, "end": v(-23.48, -22.74) * mm});
            skLineSegment(sketch, "E15.22.1", {"start": v(-23.55, -21.2) * mm, "end": v(-22.8, -20.53) * mm});
            skLineSegment(sketch, "E15.22.2", {"start": v(-22.4, -22.4) * mm, "end": v(-21.7, -21.7) * mm});
            skPoint(sketch, "E15.22.3", {"position": v(-23.97, -22.4) * mm});
            skPoint(sketch, "E15.22.4", {"position": v(-23.6, -21.24) * mm});
            skArc(sketch, "E15.22.5", {"start": v(-23.62, -21.3) * mm, "mid": v(-23.8, -21.77) * mm, "end": v(-23.94, -22.26) * mm});
            skPoint(sketch, "E15.22.6", {"position": v(-23.62, -22.77) * mm});
            skPoint(sketch, "E15.22.7", {"position": v(-22.45, -22.45) * mm});
            skArc(sketch, "E15.22.8", {"start": v(-23.94, -22.26) * mm, "mid": v(-23.94, -22.38) * mm, "end": v(-23.88, -22.5) * mm});
            skArc(sketch, "E15.22.9", {"start": v(-23.71, -22.67) * mm, "mid": v(-23.6, -22.73) * mm, "end": v(-23.48, -22.74) * mm});
            skArc(sketch, "E15.22.10", {"start": v(-23.71, -22.67) * mm, "mid": v(-23.75, -22.62) * mm, "end": v(-23.8, -22.58) * mm});
            skArc(sketch, "E15.22.11", {"start": v(-23.88, -22.5) * mm, "mid": v(-23.84, -22.54) * mm, "end": v(-23.8, -22.58) * mm});
            skArc(sketch, "E15.22.12", {"start": v(-22.5, -22.47) * mm, "mid": v(-22.45, -22.45) * mm, "end": v(-22.4, -22.4) * mm});
            skArc(sketch, "E15.22.13", {"start": v(-23.55, -21.2) * mm, "mid": v(-23.59, -21.25) * mm, "end": v(-23.62, -21.3) * mm});
            skArc(sketch, "E15.23.0", {"start": v(-20.03, -24.7) * mm, "mid": v(-20.5, -24.9) * mm, "end": v(-20.97, -25.07) * mm});
            skLineSegment(sketch, "E15.23.1", {"start": v(-21.2, -23.55) * mm, "end": v(-20.53, -22.8) * mm});
            skLineSegment(sketch, "E15.23.2", {"start": v(-19.94, -24.63) * mm, "end": v(-19.3, -23.85) * mm});
            skPoint(sketch, "E15.23.3", {"position": v(-21.5, -24.78) * mm});
            skPoint(sketch, "E15.23.4", {"position": v(-21.24, -23.6) * mm});
            skArc(sketch, "E15.23.5", {"start": v(-21.26, -23.65) * mm, "mid": v(-21.39, -24.14) * mm, "end": v(-21.48, -24.64) * mm});
            skPoint(sketch, "E15.23.6", {"position": v(-21.1, -25.11) * mm});
            skPoint(sketch, "E15.23.7", {"position": v(-19.98, -24.67) * mm});
            skArc(sketch, "E15.23.8", {"start": v(-21.48, -24.64) * mm, "mid": v(-21.47, -24.76) * mm, "end": v(-21.4, -24.87) * mm});
            skArc(sketch, "E15.23.9", {"start": v(-21.22, -25.02) * mm, "mid": v(-21.1, -25.08) * mm, "end": v(-20.97, -25.07) * mm});
            skArc(sketch, "E15.23.10", {"start": v(-21.22, -25.02) * mm, "mid": v(-21.26, -24.98) * mm, "end": v(-21.3, -24.94) * mm});
            skArc(sketch, "E15.23.11", {"start": v(-21.4, -24.87) * mm, "mid": v(-21.35, -24.9) * mm, "end": v(-21.3, -24.94) * mm});
            skArc(sketch, "E15.23.12", {"start": v(-20.03, -24.7) * mm, "mid": v(-19.99, -24.67) * mm, "end": v(-19.94, -24.63) * mm});
            skArc(sketch, "E15.23.13", {"start": v(-21.2, -23.55) * mm, "mid": v(-21.24, -23.6) * mm, "end": v(-21.26, -23.65) * mm});
            skArc(sketch, "E15.24.0", {"start": v(-17.34, -26.66) * mm, "mid": v(-17.78, -26.9) * mm, "end": v(-18.24, -27.12) * mm});
            skLineSegment(sketch, "E15.24.1", {"start": v(-18.63, -25.64) * mm, "end": v(-18.04, -24.82) * mm});
            skLineSegment(sketch, "E15.24.2", {"start": v(-17.26, -26.58) * mm, "end": v(-16.71, -25.73) * mm});
            skPoint(sketch, "E15.24.3", {"position": v(-18.8, -26.89) * mm});
            skPoint(sketch, "E15.24.4", {"position": v(-18.66, -25.69) * mm});
            skArc(sketch, "E15.24.5", {"start": v(-18.67, -25.74) * mm, "mid": v(-18.75, -26.24) * mm, "end": v(-18.79, -26.75) * mm});
            skPoint(sketch, "E15.24.6", {"position": v(-18.37, -27.18) * mm});
            skPoint(sketch, "E15.24.7", {"position": v(-17.3, -26.63) * mm});
            skArc(sketch, "E15.24.8", {"start": v(-18.79, -26.75) * mm, "mid": v(-18.76, -26.87) * mm, "end": v(-18.68, -26.97) * mm});
            skArc(sketch, "E15.24.9", {"start": v(-18.48, -27.1) * mm, "mid": v(-18.36, -27.14) * mm, "end": v(-18.24, -27.12) * mm});
            skArc(sketch, "E15.24.10", {"start": v(-18.48, -27.1) * mm, "mid": v(-18.53, -27.07) * mm, "end": v(-18.58, -27.03) * mm});
            skArc(sketch, "E15.24.11", {"start": v(-18.68, -26.97) * mm, "mid": v(-18.63, -27) * mm, "end": v(-18.58, -27.03) * mm});
            skArc(sketch, "E15.24.12", {"start": v(-17.34, -26.66) * mm, "mid": v(-17.3, -26.62) * mm, "end": v(-17.26, -26.58) * mm});
            skArc(sketch, "E15.24.13", {"start": v(-18.63, -25.64) * mm, "mid": v(-18.66, -25.69) * mm, "end": v(-18.67, -25.74) * mm});
            skArc(sketch, "E15.25.0", {"start": v(-14.46, -28.33) * mm, "mid": v(-14.87, -28.62) * mm, "end": v(-15.3, -28.88) * mm});
            skLineSegment(sketch, "E15.25.1", {"start": v(-15.85, -27.45) * mm, "end": v(-15.34, -26.57) * mm});
            skLineSegment(sketch, "E15.25.2", {"start": v(-14.39, -28.24) * mm, "end": v(-13.93, -27.34) * mm});
            skPoint(sketch, "E15.25.3", {"position": v(-15.88, -28.7) * mm});
            skPoint(sketch, "E15.25.4", {"position": v(-15.87, -27.5) * mm});
            skArc(sketch, "E15.25.5", {"start": v(-15.88, -27.56) * mm, "mid": v(-15.9, -28.06) * mm, "end": v(-15.89, -28.56) * mm});
            skPoint(sketch, "E15.25.6", {"position": v(-15.43, -28.95) * mm});
            skPoint(sketch, "E15.25.7", {"position": v(-14.41, -28.29) * mm});
            skArc(sketch, "E15.25.8", {"start": v(-15.89, -28.56) * mm, "mid": v(-15.85, -28.69) * mm, "end": v(-15.76, -28.77) * mm});
            skArc(sketch, "E15.25.9", {"start": v(-15.55, -28.88) * mm, "mid": v(-15.43, -28.91) * mm, "end": v(-15.3, -28.88) * mm});
            skArc(sketch, "E15.25.10", {"start": v(-15.55, -28.88) * mm, "mid": v(-15.6, -28.86) * mm, "end": v(-15.65, -28.83) * mm});
            skArc(sketch, "E15.25.11", {"start": v(-15.76, -28.77) * mm, "mid": v(-15.7, -28.8) * mm, "end": v(-15.65, -28.83) * mm});
            skArc(sketch, "E15.25.12", {"start": v(-14.46, -28.33) * mm, "mid": v(-14.42, -28.29) * mm, "end": v(-14.39, -28.24) * mm});
            skArc(sketch, "E15.25.13", {"start": v(-15.85, -27.45) * mm, "mid": v(-15.87, -27.5) * mm, "end": v(-15.88, -27.56) * mm});
            skArc(sketch, "E15.26.0", {"start": v(-11.42, -29.68) * mm, "mid": v(-11.8, -30.01) * mm, "end": v(-12.2, -30.32) * mm});
            skLineSegment(sketch, "E15.26.1", {"start": v(-12.9, -28.95) * mm, "end": v(-12.48, -28.03) * mm});
            skLineSegment(sketch, "E15.26.2", {"start": v(-11.36, -29.59) * mm, "end": v(-11, -28.65) * mm});
            skPoint(sketch, "E15.26.3", {"position": v(-12.8, -30.2) * mm});
            skPoint(sketch, "E15.26.4", {"position": v(-12.91, -29) * mm});
            skArc(sketch, "E15.26.5", {"start": v(-12.91, -29.06) * mm, "mid": v(-12.88, -29.57) * mm, "end": v(-12.81, -30.07) * mm});
            skPoint(sketch, "E15.26.6", {"position": v(-12.32, -30.4) * mm});
            skPoint(sketch, "E15.26.7", {"position": v(-11.38, -29.64) * mm});
            skArc(sketch, "E15.26.8", {"start": v(-12.81, -30.07) * mm, "mid": v(-12.76, -30.18) * mm, "end": v(-12.66, -30.26) * mm});
            skArc(sketch, "E15.26.9", {"start": v(-12.45, -30.35) * mm, "mid": v(-12.32, -30.37) * mm, "end": v(-12.2, -30.32) * mm});
            skArc(sketch, "E15.26.10", {"start": v(-12.45, -30.35) * mm, "mid": v(-12.5, -30.33) * mm, "end": v(-12.55, -30.3) * mm});
            skArc(sketch, "E15.26.11", {"start": v(-12.66, -30.26) * mm, "mid": v(-12.6, -30.28) * mm, "end": v(-12.55, -30.3) * mm});
            skArc(sketch, "E15.26.12", {"start": v(-11.42, -29.68) * mm, "mid": v(-11.38, -29.64) * mm, "end": v(-11.36, -29.59) * mm});
            skArc(sketch, "E15.26.13", {"start": v(-12.9, -28.95) * mm, "mid": v(-12.9, -29) * mm, "end": v(-12.91, -29.06) * mm});
            skArc(sketch, "E15.27.0", {"start": v(-8.26, -30.71) * mm, "mid": v(-8.6, -31.08) * mm, "end": v(-8.96, -31.43) * mm});
            skLineSegment(sketch, "E15.27.1", {"start": v(-9.8, -30.14) * mm, "end": v(-9.48, -29.18) * mm});
            skLineSegment(sketch, "E15.27.2", {"start": v(-8.2, -30.61) * mm, "end": v(-7.94, -29.64) * mm});
            skPoint(sketch, "E15.27.3", {"position": v(-9.56, -31.38) * mm});
            skPoint(sketch, "E15.27.4", {"position": v(-9.81, -30.2) * mm});
            skArc(sketch, "E15.27.5", {"start": v(-9.8, -30.25) * mm, "mid": v(-9.72, -30.75) * mm, "end": v(-9.6, -31.24) * mm});
            skPoint(sketch, "E15.27.6", {"position": v(-9.07, -31.53) * mm});
            skPoint(sketch, "E15.27.7", {"position": v(-8.22, -30.67) * mm});
            skArc(sketch, "E15.27.8", {"start": v(-9.6, -31.24) * mm, "mid": v(-9.54, -31.35) * mm, "end": v(-9.43, -31.42) * mm});
            skArc(sketch, "E15.27.9", {"start": v(-9.2, -31.49) * mm, "mid": v(-9.08, -31.5) * mm, "end": v(-8.96, -31.43) * mm});
            skArc(sketch, "E15.27.10", {"start": v(-9.2, -31.49) * mm, "mid": v(-9.26, -31.47) * mm, "end": v(-9.32, -31.45) * mm});
            skArc(sketch, "E15.27.11", {"start": v(-9.43, -31.42) * mm, "mid": v(-9.37, -31.44) * mm, "end": v(-9.32, -31.45) * mm});
            skArc(sketch, "E15.27.12", {"start": v(-8.26, -30.71) * mm, "mid": v(-8.22, -30.67) * mm, "end": v(-8.2, -30.61) * mm});
            skArc(sketch, "E15.27.13", {"start": v(-9.8, -30.14) * mm, "mid": v(-9.8, -30.2) * mm, "end": v(-9.8, -30.25) * mm});
            skArc(sketch, "E15.28.0", {"start": v(-5, -31.4) * mm, "mid": v(-5.3, -31.81) * mm, "end": v(-5.63, -32.2) * mm});
            skLineSegment(sketch, "E15.28.1", {"start": v(-6.59, -31) * mm, "end": v(-6.38, -30.01) * mm});
            skLineSegment(sketch, "E15.28.2", {"start": v(-4.96, -31.3) * mm, "end": v(-4.8, -30.3) * mm});
            skPoint(sketch, "E15.28.3", {"position": v(-6.23, -32.2) * mm});
            skPoint(sketch, "E15.28.4", {"position": v(-6.6, -31.06) * mm});
            skArc(sketch, "E15.28.5", {"start": v(-6.59, -31.11) * mm, "mid": v(-6.45, -31.6) * mm, "end": v(-6.28, -32.08) * mm});
            skPoint(sketch, "E15.28.6", {"position": v(-5.73, -32.3) * mm});
            skPoint(sketch, "E15.28.7", {"position": v(-4.97, -31.36) * mm});
            skArc(sketch, "E15.28.8", {"start": v(-6.28, -32.08) * mm, "mid": v(-6.2, -32.18) * mm, "end": v(-6.1, -32.23) * mm});
            skArc(sketch, "E15.28.9", {"start": v(-5.86, -32.28) * mm, "mid": v(-5.74, -32.27) * mm, "end": v(-5.63, -32.2) * mm});
            skArc(sketch, "E15.28.10", {"start": v(-5.86, -32.28) * mm, "mid": v(-5.92, -32.27) * mm, "end": v(-5.98, -32.25) * mm});
            skArc(sketch, "E15.28.11", {"start": v(-6.1, -32.23) * mm, "mid": v(-6.04, -32.24) * mm, "end": v(-5.98, -32.25) * mm});
            skArc(sketch, "E15.28.12", {"start": v(-5, -31.4) * mm, "mid": v(-4.97, -31.36) * mm, "end": v(-4.96, -31.3) * mm});
            skArc(sketch, "E15.28.13", {"start": v(-6.59, -31) * mm, "mid": v(-6.6, -31.06) * mm, "end": v(-6.59, -31.11) * mm});
            skArc(sketch, "E15.29.0", {"start": v(-1.69, -31.76) * mm, "mid": v(-1.95, -32.2) * mm, "end": v(-2.23, -32.6) * mm});
            skLineSegment(sketch, "E15.29.1", {"start": v(-3.31, -31.52) * mm, "end": v(-3.2, -30.52) * mm});
            skLineSegment(sketch, "E15.29.2", {"start": v(-1.66, -31.65) * mm, "end": v(-1.6, -30.64) * mm});
            skPoint(sketch, "E15.29.3", {"position": v(-2.83, -32.68) * mm});
            skPoint(sketch, "E15.29.4", {"position": v(-3.32, -31.58) * mm});
            skArc(sketch, "E15.29.5", {"start": v(-3.3, -31.63) * mm, "mid": v(-3.11, -32.1) * mm, "end": v(-2.9, -32.56) * mm});
            skPoint(sketch, "E15.29.6", {"position": v(-2.32, -32.72) * mm});
            skPoint(sketch, "E15.29.7", {"position": v(-1.66, -31.7) * mm});
            skArc(sketch, "E15.29.8", {"start": v(-2.9, -32.56) * mm, "mid": v(-2.81, -32.65) * mm, "end": v(-2.7, -32.7) * mm});
            skArc(sketch, "E15.29.9", {"start": v(-2.46, -32.71) * mm, "mid": v(-2.33, -32.69) * mm, "end": v(-2.23, -32.6) * mm});
            skArc(sketch, "E15.29.10", {"start": v(-2.46, -32.71) * mm, "mid": v(-2.52, -32.7) * mm, "end": v(-2.57, -32.7) * mm});
            skArc(sketch, "E15.29.11", {"start": v(-2.7, -32.7) * mm, "mid": v(-2.63, -32.7) * mm, "end": v(-2.57, -32.7) * mm});
            skArc(sketch, "E15.29.12", {"start": v(-1.69, -31.76) * mm, "mid": v(-1.67, -31.7) * mm, "end": v(-1.66, -31.65) * mm});
            skArc(sketch, "E15.29.13", {"start": v(-3.31, -31.52) * mm, "mid": v(-3.31, -31.58) * mm, "end": v(-3.3, -31.63) * mm});
            skArc(sketch, "E15.30.0", {"start": v(1.64, -31.76) * mm, "mid": v(1.43, -32.22) * mm, "end": v(1.19, -32.66) * mm});
            skLineSegment(sketch, "E15.30.1", {"start": v(0, -31.7) * mm, "end": v(0, -30.68) * mm});
            skLineSegment(sketch, "E15.30.2", {"start": v(1.66, -31.65) * mm, "end": v(1.6, -30.64) * mm});
            skPoint(sketch, "E15.30.3", {"position": v(0.6, -32.8) * mm});
            skPoint(sketch, "E15.30.4", {"position": v(0, -31.75) * mm});
            skArc(sketch, "E15.30.5", {"start": v(0.03, -31.8) * mm, "mid": v(0.26, -32.25) * mm, "end": v(0.52, -32.68) * mm});
            skPoint(sketch, "E15.30.6", {"position": v(1.12, -32.79) * mm});
            skPoint(sketch, "E15.30.7", {"position": v(1.66, -31.7) * mm});
            skArc(sketch, "E15.30.8", {"start": v(0.52, -32.68) * mm, "mid": v(0.62, -32.77) * mm, "end": v(0.74, -32.8) * mm});
            skArc(sketch, "E15.30.9", {"start": v(0.98, -32.79) * mm, "mid": v(1.1, -32.75) * mm, "end": v(1.19, -32.66) * mm});
            skArc(sketch, "E15.30.10", {"start": v(0.98, -32.79) * mm, "mid": v(0.92, -32.8) * mm, "end": v(0.86, -32.8) * mm});
            skArc(sketch, "E15.30.11", {"start": v(0.74, -32.8) * mm, "mid": v(0.8, -32.8) * mm, "end": v(0.86, -32.8) * mm});
            skArc(sketch, "E15.30.12", {"start": v(1.64, -31.76) * mm, "mid": v(1.66, -31.7) * mm, "end": v(1.66, -31.65) * mm});
            skArc(sketch, "E15.30.13", {"start": v(0, -31.7) * mm, "mid": v(0, -31.75) * mm, "end": v(0.03, -31.8) * mm});
            skArc(sketch, "E15.31.0", {"start": v(4.95, -31.42) * mm, "mid": v(4.79, -31.9) * mm, "end": v(4.6, -32.36) * mm});
            skLineSegment(sketch, "E15.31.1", {"start": v(3.31, -31.52) * mm, "end": v(3.2, -30.52) * mm});
            skLineSegment(sketch, "E15.31.2", {"start": v(4.96, -31.3) * mm, "end": v(4.8, -30.3) * mm});
            skPoint(sketch, "E15.31.3", {"position": v(4.03, -32.56) * mm});
            skPoint(sketch, "E15.31.4", {"position": v(3.32, -31.58) * mm});
            skArc(sketch, "E15.31.5", {"start": v(3.35, -31.63) * mm, "mid": v(3.63, -32.05) * mm, "end": v(3.94, -32.45) * mm});
            skPoint(sketch, "E15.31.6", {"position": v(4.54, -32.49) * mm});
            skPoint(sketch, "E15.31.7", {"position": v(4.97, -31.36) * mm});
            skArc(sketch, "E15.31.8", {"start": v(3.94, -32.45) * mm, "mid": v(4.04, -32.52) * mm, "end": v(4.17, -32.54) * mm});
            skArc(sketch, "E15.31.9", {"start": v(4.4, -32.5) * mm, "mid": v(4.52, -32.46) * mm, "end": v(4.6, -32.36) * mm});
            skArc(sketch, "E15.31.10", {"start": v(4.4, -32.5) * mm, "mid": v(4.34, -32.52) * mm, "end": v(4.28, -32.52) * mm});
            skArc(sketch, "E15.31.11", {"start": v(4.17, -32.54) * mm, "mid": v(4.22, -32.53) * mm, "end": v(4.28, -32.52) * mm});
            skArc(sketch, "E15.31.12", {"start": v(4.95, -31.42) * mm, "mid": v(4.96, -31.36) * mm, "end": v(4.96, -31.3) * mm});
            skArc(sketch, "E15.31.13", {"start": v(3.31, -31.52) * mm, "mid": v(3.33, -31.57) * mm, "end": v(3.35, -31.63) * mm});
            skArc(sketch, "E15.32.0", {"start": v(8.2, -30.73) * mm, "mid": v(8.1, -31.22) * mm, "end": v(7.95, -31.7) * mm});
            skLineSegment(sketch, "E15.32.1", {"start": v(6.59, -31) * mm, "end": v(6.38, -30.01) * mm});
            skLineSegment(sketch, "E15.32.2", {"start": v(8.2, -30.61) * mm, "end": v(7.94, -29.64) * mm});
            skPoint(sketch, "E15.32.3", {"position": v(7.4, -31.96) * mm});
            skPoint(sketch, "E15.32.4", {"position": v(6.6, -31.06) * mm});
            skArc(sketch, "E15.32.5", {"start": v(6.64, -31.1) * mm, "mid": v(6.96, -31.5) * mm, "end": v(7.3, -31.86) * mm});
            skPoint(sketch, "E15.32.6", {"position": v(7.9, -31.84) * mm});
            skPoint(sketch, "E15.32.7", {"position": v(8.22, -30.67) * mm});
            skArc(sketch, "E15.32.8", {"start": v(7.3, -31.86) * mm, "mid": v(7.42, -31.92) * mm, "end": v(7.54, -31.92) * mm});
            skArc(sketch, "E15.32.9", {"start": v(7.77, -31.87) * mm, "mid": v(7.88, -31.8) * mm, "end": v(7.95, -31.7) * mm});
            skArc(sketch, "E15.32.10", {"start": v(7.77, -31.87) * mm, "mid": v(7.71, -31.88) * mm, "end": v(7.66, -31.9) * mm});
            skArc(sketch, "E15.32.11", {"start": v(7.54, -31.92) * mm, "mid": v(7.6, -31.91) * mm, "end": v(7.66, -31.9) * mm});
            skArc(sketch, "E15.32.12", {"start": v(8.2, -30.73) * mm, "mid": v(8.21, -30.67) * mm, "end": v(8.2, -30.61) * mm});
            skArc(sketch, "E15.32.13", {"start": v(6.59, -31) * mm, "mid": v(6.6, -31.05) * mm, "end": v(6.64, -31.1) * mm});
            skArc(sketch, "E15.33.0", {"start": v(11.37, -29.7) * mm, "mid": v(11.31, -30.2) * mm, "end": v(11.22, -30.7) * mm});
            skLineSegment(sketch, "E15.33.1", {"start": v(9.8, -30.14) * mm, "end": v(9.48, -29.18) * mm});
            skLineSegment(sketch, "E15.33.2", {"start": v(11.36, -29.59) * mm, "end": v(11, -28.65) * mm});
            skPoint(sketch, "E15.33.3", {"position": v(10.7, -31) * mm});
            skPoint(sketch, "E15.33.4", {"position": v(9.81, -30.2) * mm});
            skArc(sketch, "E15.33.5", {"start": v(9.85, -30.24) * mm, "mid": v(10.21, -30.6) * mm, "end": v(10.6, -30.92) * mm});
            skPoint(sketch, "E15.33.6", {"position": v(11.2, -30.84) * mm});
            skPoint(sketch, "E15.33.7", {"position": v(11.38, -29.64) * mm});
            skArc(sketch, "E15.33.8", {"start": v(10.6, -30.92) * mm, "mid": v(10.71, -30.97) * mm, "end": v(10.84, -30.96) * mm});
            skArc(sketch, "E15.33.9", {"start": v(11.06, -30.88) * mm, "mid": v(11.17, -30.81) * mm, "end": v(11.22, -30.7) * mm});
            skArc(sketch, "E15.33.10", {"start": v(11.06, -30.88) * mm, "mid": v(11, -30.9) * mm, "end": v(10.95, -30.92) * mm});
            skArc(sketch, "E15.33.11", {"start": v(10.84, -30.96) * mm, "mid": v(10.9, -30.94) * mm, "end": v(10.95, -30.92) * mm});
            skArc(sketch, "E15.33.12", {"start": v(11.37, -29.7) * mm, "mid": v(11.37, -29.64) * mm, "end": v(11.36, -29.59) * mm});
            skArc(sketch, "E15.33.13", {"start": v(9.8, -30.14) * mm, "mid": v(9.82, -30.2) * mm, "end": v(9.85, -30.24) * mm});
            skArc(sketch, "E15.34.0", {"start": v(14.42, -28.35) * mm, "mid": v(14.4, -28.85) * mm, "end": v(14.37, -29.36) * mm});
            skLineSegment(sketch, "E15.34.1", {"start": v(12.9, -28.95) * mm, "end": v(12.48, -28.03) * mm});
            skLineSegment(sketch, "E15.34.2", {"start": v(14.39, -28.24) * mm, "end": v(13.93, -27.34) * mm});
            skPoint(sketch, "E15.34.3", {"position": v(13.9, -29.72) * mm});
            skPoint(sketch, "E15.34.4", {"position": v(12.91, -29) * mm});
            skArc(sketch, "E15.34.5", {"start": v(12.96, -29.04) * mm, "mid": v(13.36, -29.36) * mm, "end": v(13.77, -29.64) * mm});
            skPoint(sketch, "E15.34.6", {"position": v(14.35, -29.5) * mm});
            skPoint(sketch, "E15.34.7", {"position": v(14.41, -28.29) * mm});
            skArc(sketch, "E15.34.8", {"start": v(13.77, -29.64) * mm, "mid": v(13.9, -29.68) * mm, "end": v(14.02, -29.66) * mm});
            skArc(sketch, "E15.34.9", {"start": v(14.23, -29.56) * mm, "mid": v(14.33, -29.48) * mm, "end": v(14.37, -29.36) * mm});
            skArc(sketch, "E15.34.10", {"start": v(14.23, -29.56) * mm, "mid": v(14.18, -29.58) * mm, "end": v(14.12, -29.6) * mm});
            skArc(sketch, "E15.34.11", {"start": v(14.02, -29.66) * mm, "mid": v(14.07, -29.63) * mm, "end": v(14.12, -29.6) * mm});
            skArc(sketch, "E15.34.12", {"start": v(14.42, -28.35) * mm, "mid": v(14.4, -28.3) * mm, "end": v(14.39, -28.24) * mm});
            skArc(sketch, "E15.34.13", {"start": v(12.9, -28.95) * mm, "mid": v(12.92, -29) * mm, "end": v(12.96, -29.04) * mm});
            skArc(sketch, "E15.35.0", {"start": v(17.3, -26.69) * mm, "mid": v(17.35, -27.19) * mm, "end": v(17.36, -27.7) * mm});
            skLineSegment(sketch, "E15.35.1", {"start": v(15.85, -27.45) * mm, "end": v(15.34, -26.57) * mm});
            skLineSegment(sketch, "E15.35.2", {"start": v(17.26, -26.58) * mm, "end": v(16.71, -25.73) * mm});
            skPoint(sketch, "E15.35.3", {"position": v(16.92, -28.1) * mm});
            skPoint(sketch, "E15.35.4", {"position": v(15.87, -27.5) * mm});
            skArc(sketch, "E15.35.5", {"start": v(15.92, -27.53) * mm, "mid": v(16.35, -27.8) * mm, "end": v(16.8, -28.04) * mm});
            skPoint(sketch, "E15.35.6", {"position": v(17.36, -27.84) * mm});
            skPoint(sketch, "E15.35.7", {"position": v(17.3, -26.63) * mm});
            skArc(sketch, "E15.35.8", {"start": v(16.8, -28.04) * mm, "mid": v(16.92, -28.07) * mm, "end": v(17.04, -28.03) * mm});
            skArc(sketch, "E15.35.9", {"start": v(17.24, -27.9) * mm, "mid": v(17.33, -27.82) * mm, "end": v(17.36, -27.7) * mm});
            skArc(sketch, "E15.35.10", {"start": v(17.24, -27.9) * mm, "mid": v(17.19, -27.94) * mm, "end": v(17.14, -27.97) * mm});
            skArc(sketch, "E15.35.11", {"start": v(17.04, -28.03) * mm, "mid": v(17.1, -28) * mm, "end": v(17.14, -27.97) * mm});
            skArc(sketch, "E15.35.12", {"start": v(17.3, -26.69) * mm, "mid": v(17.29, -26.63) * mm, "end": v(17.26, -26.58) * mm});
            skArc(sketch, "E15.35.13", {"start": v(15.85, -27.45) * mm, "mid": v(15.88, -27.5) * mm, "end": v(15.92, -27.53) * mm});
            skArc(sketch, "E15.36.0", {"start": v(20, -24.73) * mm, "mid": v(20.1, -25.23) * mm, "end": v(20.16, -25.73) * mm});
            skLineSegment(sketch, "E15.36.1", {"start": v(18.63, -25.64) * mm, "end": v(18.04, -24.82) * mm});
            skLineSegment(sketch, "E15.36.2", {"start": v(19.94, -24.63) * mm, "end": v(19.3, -23.85) * mm});
            skPoint(sketch, "E15.36.3", {"position": v(19.77, -26.18) * mm});
            skPoint(sketch, "E15.36.4", {"position": v(18.66, -25.69) * mm});
            skArc(sketch, "E15.36.5", {"start": v(18.71, -25.71) * mm, "mid": v(19.17, -25.94) * mm, "end": v(19.63, -26.13) * mm});
            skPoint(sketch, "E15.36.6", {"position": v(20.17, -25.87) * mm});
            skPoint(sketch, "E15.36.7", {"position": v(19.98, -24.67) * mm});
            skArc(sketch, "E15.36.8", {"start": v(19.63, -26.13) * mm, "mid": v(19.76, -26.15) * mm, "end": v(19.88, -26.1) * mm});
            skArc(sketch, "E15.36.9", {"start": v(20.06, -25.95) * mm, "mid": v(20.14, -25.85) * mm, "end": v(20.16, -25.73) * mm});
            skArc(sketch, "E15.36.10", {"start": v(20.06, -25.95) * mm, "mid": v(20.02, -25.99) * mm, "end": v(19.97, -26.03) * mm});
            skArc(sketch, "E15.36.11", {"start": v(19.88, -26.1) * mm, "mid": v(19.92, -26.06) * mm, "end": v(19.97, -26.03) * mm});
            skArc(sketch, "E15.36.12", {"start": v(20, -24.73) * mm, "mid": v(19.98, -24.68) * mm, "end": v(19.94, -24.63) * mm});
            skArc(sketch, "E15.36.13", {"start": v(18.63, -25.64) * mm, "mid": v(18.67, -25.68) * mm, "end": v(18.71, -25.71) * mm});
            skArc(sketch, "E15.37.0", {"start": v(22.47, -22.5) * mm, "mid": v(22.62, -22.99) * mm, "end": v(22.74, -23.48) * mm});
            skLineSegment(sketch, "E15.37.1", {"start": v(21.2, -23.55) * mm, "end": v(20.53, -22.8) * mm});
            skLineSegment(sketch, "E15.37.2", {"start": v(22.4, -22.4) * mm, "end": v(21.7, -21.7) * mm});
            skPoint(sketch, "E15.37.3", {"position": v(22.4, -23.97) * mm});
            skPoint(sketch, "E15.37.4", {"position": v(21.24, -23.6) * mm});
            skArc(sketch, "E15.37.5", {"start": v(21.3, -23.62) * mm, "mid": v(21.77, -23.8) * mm, "end": v(22.26, -23.94) * mm});
            skPoint(sketch, "E15.37.6", {"position": v(22.77, -23.62) * mm});
            skPoint(sketch, "E15.37.7", {"position": v(22.45, -22.45) * mm});
            skArc(sketch, "E15.37.8", {"start": v(22.26, -23.94) * mm, "mid": v(22.38, -23.94) * mm, "end": v(22.5, -23.88) * mm});
            skArc(sketch, "E15.37.9", {"start": v(22.67, -23.71) * mm, "mid": v(22.73, -23.6) * mm, "end": v(22.74, -23.48) * mm});
            skArc(sketch, "E15.37.10", {"start": v(22.67, -23.71) * mm, "mid": v(22.62, -23.75) * mm, "end": v(22.58, -23.8) * mm});
            skArc(sketch, "E15.37.11", {"start": v(22.5, -23.88) * mm, "mid": v(22.54, -23.84) * mm, "end": v(22.58, -23.8) * mm});
            skArc(sketch, "E15.37.12", {"start": v(22.47, -22.5) * mm, "mid": v(22.45, -22.45) * mm, "end": v(22.4, -22.4) * mm});
            skArc(sketch, "E15.37.13", {"start": v(21.2, -23.55) * mm, "mid": v(21.25, -23.59) * mm, "end": v(21.3, -23.62) * mm});
            skArc(sketch, "E15.38.0", {"start": v(24.7, -20.03) * mm, "mid": v(24.9, -20.5) * mm, "end": v(25.07, -20.97) * mm});
            skLineSegment(sketch, "E15.38.1", {"start": v(23.55, -21.2) * mm, "end": v(22.8, -20.53) * mm});
            skLineSegment(sketch, "E15.38.2", {"start": v(24.63, -19.94) * mm, "end": v(23.85, -19.3) * mm});
            skPoint(sketch, "E15.38.3", {"position": v(24.78, -21.5) * mm});
            skPoint(sketch, "E15.38.4", {"position": v(23.6, -21.24) * mm});
            skArc(sketch, "E15.38.5", {"start": v(23.65, -21.26) * mm, "mid": v(24.14, -21.39) * mm, "end": v(24.64, -21.48) * mm});
            skPoint(sketch, "E15.38.6", {"position": v(25.11, -21.1) * mm});
            skPoint(sketch, "E15.38.7", {"position": v(24.67, -19.98) * mm});
            skArc(sketch, "E15.38.8", {"start": v(24.64, -21.48) * mm, "mid": v(24.76, -21.47) * mm, "end": v(24.87, -21.4) * mm});
            skArc(sketch, "E15.38.9", {"start": v(25.02, -21.22) * mm, "mid": v(25.08, -21.1) * mm, "end": v(25.07, -20.97) * mm});
            skArc(sketch, "E15.38.10", {"start": v(25.02, -21.22) * mm, "mid": v(24.98, -21.26) * mm, "end": v(24.94, -21.3) * mm});
            skArc(sketch, "E15.38.11", {"start": v(24.87, -21.4) * mm, "mid": v(24.9, -21.35) * mm, "end": v(24.94, -21.3) * mm});
            skArc(sketch, "E15.38.12", {"start": v(24.7, -20.03) * mm, "mid": v(24.67, -19.99) * mm, "end": v(24.63, -19.94) * mm});
            skArc(sketch, "E15.38.13", {"start": v(23.55, -21.2) * mm, "mid": v(23.6, -21.24) * mm, "end": v(23.65, -21.26) * mm});
            skArc(sketch, "E15.39.0", {"start": v(26.66, -17.34) * mm, "mid": v(26.9, -17.78) * mm, "end": v(27.12, -18.24) * mm});
            skLineSegment(sketch, "E15.39.1", {"start": v(25.64, -18.63) * mm, "end": v(24.82, -18.04) * mm});
            skLineSegment(sketch, "E15.39.2", {"start": v(26.58, -17.26) * mm, "end": v(25.73, -16.71) * mm});
            skPoint(sketch, "E15.39.3", {"position": v(26.89, -18.8) * mm});
            skPoint(sketch, "E15.39.4", {"position": v(25.69, -18.66) * mm});
            skArc(sketch, "E15.39.5", {"start": v(25.74, -18.67) * mm, "mid": v(26.24, -18.75) * mm, "end": v(26.75, -18.79) * mm});
            skPoint(sketch, "E15.39.6", {"position": v(27.18, -18.37) * mm});
            skPoint(sketch, "E15.39.7", {"position": v(26.63, -17.3) * mm});
            skArc(sketch, "E15.39.8", {"start": v(26.75, -18.79) * mm, "mid": v(26.87, -18.76) * mm, "end": v(26.97, -18.68) * mm});
            skArc(sketch, "E15.39.9", {"start": v(27.1, -18.48) * mm, "mid": v(27.14, -18.36) * mm, "end": v(27.12, -18.24) * mm});
            skArc(sketch, "E15.39.10", {"start": v(27.1, -18.48) * mm, "mid": v(27.07, -18.53) * mm, "end": v(27.03, -18.58) * mm});
            skArc(sketch, "E15.39.11", {"start": v(26.97, -18.68) * mm, "mid": v(27, -18.63) * mm, "end": v(27.03, -18.58) * mm});
            skArc(sketch, "E15.39.12", {"start": v(26.66, -17.34) * mm, "mid": v(26.62, -17.3) * mm, "end": v(26.58, -17.26) * mm});
            skArc(sketch, "E15.39.13", {"start": v(25.64, -18.63) * mm, "mid": v(25.69, -18.66) * mm, "end": v(25.74, -18.67) * mm});
            skArc(sketch, "E15.40.0", {"start": v(28.33, -14.46) * mm, "mid": v(28.62, -14.87) * mm, "end": v(28.88, -15.3) * mm});
            skLineSegment(sketch, "E15.40.1", {"start": v(27.45, -15.85) * mm, "end": v(26.57, -15.34) * mm});
            skLineSegment(sketch, "E15.40.2", {"start": v(28.24, -14.39) * mm, "end": v(27.34, -13.93) * mm});
            skPoint(sketch, "E15.40.3", {"position": v(28.7, -15.88) * mm});
            skPoint(sketch, "E15.40.4", {"position": v(27.5, -15.88) * mm});
            skArc(sketch, "E15.40.5", {"start": v(27.56, -15.88) * mm, "mid": v(28.06, -15.9) * mm, "end": v(28.56, -15.89) * mm});
            skPoint(sketch, "E15.40.6", {"position": v(28.95, -15.43) * mm});
            skPoint(sketch, "E15.40.7", {"position": v(28.29, -14.41) * mm});
            skArc(sketch, "E15.40.8", {"start": v(28.56, -15.89) * mm, "mid": v(28.69, -15.85) * mm, "end": v(28.77, -15.76) * mm});
            skArc(sketch, "E15.40.9", {"start": v(28.88, -15.55) * mm, "mid": v(28.91, -15.43) * mm, "end": v(28.88, -15.3) * mm});
            skArc(sketch, "E15.40.10", {"start": v(28.88, -15.55) * mm, "mid": v(28.86, -15.6) * mm, "end": v(28.83, -15.65) * mm});
            skArc(sketch, "E15.40.11", {"start": v(28.77, -15.76) * mm, "mid": v(28.8, -15.7) * mm, "end": v(28.83, -15.65) * mm});
            skArc(sketch, "E15.40.12", {"start": v(28.33, -14.46) * mm, "mid": v(28.29, -14.42) * mm, "end": v(28.24, -14.39) * mm});
            skArc(sketch, "E15.40.13", {"start": v(27.45, -15.85) * mm, "mid": v(27.5, -15.87) * mm, "end": v(27.56, -15.88) * mm});
            skArc(sketch, "E15.41.0", {"start": v(29.68, -11.42) * mm, "mid": v(30.01, -11.8) * mm, "end": v(30.32, -12.2) * mm});
            skLineSegment(sketch, "E15.41.1", {"start": v(28.95, -12.9) * mm, "end": v(28.03, -12.48) * mm});
            skLineSegment(sketch, "E15.41.2", {"start": v(29.59, -11.36) * mm, "end": v(28.65, -11) * mm});
            skPoint(sketch, "E15.41.3", {"position": v(30.2, -12.8) * mm});
            skPoint(sketch, "E15.41.4", {"position": v(29, -12.91) * mm});
            skArc(sketch, "E15.41.5", {"start": v(29.06, -12.91) * mm, "mid": v(29.57, -12.88) * mm, "end": v(30.07, -12.81) * mm});
            skPoint(sketch, "E15.41.6", {"position": v(30.4, -12.32) * mm});
            skPoint(sketch, "E15.41.7", {"position": v(29.64, -11.38) * mm});
            skArc(sketch, "E15.41.8", {"start": v(30.07, -12.81) * mm, "mid": v(30.18, -12.76) * mm, "end": v(30.26, -12.66) * mm});
            skArc(sketch, "E15.41.9", {"start": v(30.35, -12.45) * mm, "mid": v(30.37, -12.32) * mm, "end": v(30.32, -12.2) * mm});
            skArc(sketch, "E15.41.10", {"start": v(30.35, -12.45) * mm, "mid": v(30.33, -12.5) * mm, "end": v(30.3, -12.55) * mm});
            skArc(sketch, "E15.41.11", {"start": v(30.26, -12.66) * mm, "mid": v(30.28, -12.6) * mm, "end": v(30.3, -12.55) * mm});
            skArc(sketch, "E15.41.12", {"start": v(29.68, -11.42) * mm, "mid": v(29.64, -11.38) * mm, "end": v(29.59, -11.36) * mm});
            skArc(sketch, "E15.41.13", {"start": v(28.95, -12.9) * mm, "mid": v(29, -12.9) * mm, "end": v(29.06, -12.91) * mm});
            skArc(sketch, "E15.42.0", {"start": v(30.71, -8.26) * mm, "mid": v(31.08, -8.6) * mm, "end": v(31.43, -8.96) * mm});
            skLineSegment(sketch, "E15.42.1", {"start": v(30.14, -9.8) * mm, "end": v(29.18, -9.48) * mm});
            skLineSegment(sketch, "E15.42.2", {"start": v(30.61, -8.2) * mm, "end": v(29.64, -7.94) * mm});
            skPoint(sketch, "E15.42.3", {"position": v(31.38, -9.56) * mm});
            skPoint(sketch, "E15.42.4", {"position": v(30.2, -9.81) * mm});
            skArc(sketch, "E15.42.5", {"start": v(30.25, -9.8) * mm, "mid": v(30.75, -9.72) * mm, "end": v(31.24, -9.6) * mm});
            skPoint(sketch, "E15.42.6", {"position": v(31.53, -9.07) * mm});
            skPoint(sketch, "E15.42.7", {"position": v(30.67, -8.22) * mm});
            skArc(sketch, "E15.42.8", {"start": v(31.24, -9.6) * mm, "mid": v(31.35, -9.54) * mm, "end": v(31.42, -9.43) * mm});
            skArc(sketch, "E15.42.9", {"start": v(31.49, -9.2) * mm, "mid": v(31.5, -9.08) * mm, "end": v(31.43, -8.96) * mm});
            skArc(sketch, "E15.42.10", {"start": v(31.49, -9.2) * mm, "mid": v(31.47, -9.26) * mm, "end": v(31.45, -9.32) * mm});
            skArc(sketch, "E15.42.11", {"start": v(31.42, -9.43) * mm, "mid": v(31.44, -9.37) * mm, "end": v(31.45, -9.32) * mm});
            skArc(sketch, "E15.42.12", {"start": v(30.71, -8.26) * mm, "mid": v(30.67, -8.22) * mm, "end": v(30.61, -8.2) * mm});
            skArc(sketch, "E15.42.13", {"start": v(30.14, -9.8) * mm, "mid": v(30.2, -9.8) * mm, "end": v(30.25, -9.8) * mm});
            skArc(sketch, "E15.43.0", {"start": v(31.4, -5) * mm, "mid": v(31.81, -5.3) * mm, "end": v(32.2, -5.63) * mm});
            skLineSegment(sketch, "E15.43.1", {"start": v(31, -6.59) * mm, "end": v(30.01, -6.38) * mm});
            skLineSegment(sketch, "E15.43.2", {"start": v(31.3, -4.96) * mm, "end": v(30.3, -4.8) * mm});
            skPoint(sketch, "E15.43.3", {"position": v(32.2, -6.23) * mm});
            skPoint(sketch, "E15.43.4", {"position": v(31.06, -6.6) * mm});
            skArc(sketch, "E15.43.5", {"start": v(31.11, -6.59) * mm, "mid": v(31.6, -6.45) * mm, "end": v(32.08, -6.28) * mm});
            skPoint(sketch, "E15.43.6", {"position": v(32.3, -5.73) * mm});
            skPoint(sketch, "E15.43.7", {"position": v(31.36, -4.97) * mm});
            skArc(sketch, "E15.43.8", {"start": v(32.08, -6.28) * mm, "mid": v(32.18, -6.2) * mm, "end": v(32.23, -6.1) * mm});
            skArc(sketch, "E15.43.9", {"start": v(32.28, -5.86) * mm, "mid": v(32.27, -5.74) * mm, "end": v(32.2, -5.63) * mm});
            skArc(sketch, "E15.43.10", {"start": v(32.28, -5.86) * mm, "mid": v(32.27, -5.92) * mm, "end": v(32.25, -5.98) * mm});
            skArc(sketch, "E15.43.11", {"start": v(32.23, -6.1) * mm, "mid": v(32.24, -6.04) * mm, "end": v(32.25, -5.98) * mm});
            skArc(sketch, "E15.43.12", {"start": v(31.4, -5) * mm, "mid": v(31.36, -4.97) * mm, "end": v(31.3, -4.96) * mm});
            skArc(sketch, "E15.43.13", {"start": v(31, -6.59) * mm, "mid": v(31.06, -6.6) * mm, "end": v(31.11, -6.59) * mm});
            skArc(sketch, "E15.44.0", {"start": v(31.76, -1.69) * mm, "mid": v(32.2, -1.95) * mm, "end": v(32.6, -2.23) * mm});
            skLineSegment(sketch, "E15.44.1", {"start": v(31.52, -3.31) * mm, "end": v(30.52, -3.2) * mm});
            skLineSegment(sketch, "E15.44.2", {"start": v(31.65, -1.66) * mm, "end": v(30.64, -1.6) * mm});
            skPoint(sketch, "E15.44.3", {"position": v(32.68, -2.83) * mm});
            skPoint(sketch, "E15.44.4", {"position": v(31.58, -3.32) * mm});
            skArc(sketch, "E15.44.5", {"start": v(31.63, -3.3) * mm, "mid": v(32.1, -3.11) * mm, "end": v(32.56, -2.9) * mm});
            skPoint(sketch, "E15.44.6", {"position": v(32.72, -2.32) * mm});
            skPoint(sketch, "E15.44.7", {"position": v(31.7, -1.66) * mm});
            skArc(sketch, "E15.44.8", {"start": v(32.56, -2.9) * mm, "mid": v(32.65, -2.81) * mm, "end": v(32.7, -2.7) * mm});
            skArc(sketch, "E15.44.9", {"start": v(32.71, -2.46) * mm, "mid": v(32.69, -2.33) * mm, "end": v(32.6, -2.23) * mm});
            skArc(sketch, "E15.44.10", {"start": v(32.71, -2.46) * mm, "mid": v(32.7, -2.52) * mm, "end": v(32.7, -2.57) * mm});
            skArc(sketch, "E15.44.11", {"start": v(32.7, -2.7) * mm, "mid": v(32.7, -2.63) * mm, "end": v(32.7, -2.57) * mm});
            skArc(sketch, "E15.44.12", {"start": v(31.76, -1.69) * mm, "mid": v(31.7, -1.67) * mm, "end": v(31.65, -1.66) * mm});
            skArc(sketch, "E15.44.13", {"start": v(31.52, -3.31) * mm, "mid": v(31.58, -3.31) * mm, "end": v(31.63, -3.3) * mm});
            skArc(sketch, "E15.45.0", {"start": v(31.76, 1.64) * mm, "mid": v(32.22, 1.43) * mm, "end": v(32.66, 1.19) * mm});
            skLineSegment(sketch, "E15.45.1", {"start": v(31.7, 0) * mm, "end": v(30.68, 0) * mm});
            skLineSegment(sketch, "E15.45.2", {"start": v(31.65, 1.66) * mm, "end": v(30.64, 1.6) * mm});
            skPoint(sketch, "E15.45.3", {"position": v(32.8, 0.6) * mm});
            skPoint(sketch, "E15.45.4", {"position": v(31.75, 0) * mm});
            skArc(sketch, "E15.45.5", {"start": v(31.8, 0.03) * mm, "mid": v(32.25, 0.26) * mm, "end": v(32.68, 0.52) * mm});
            skPoint(sketch, "E15.45.6", {"position": v(32.79, 1.12) * mm});
            skPoint(sketch, "E15.45.7", {"position": v(31.7, 1.66) * mm});
            skArc(sketch, "E15.45.8", {"start": v(32.68, 0.52) * mm, "mid": v(32.77, 0.62) * mm, "end": v(32.8, 0.74) * mm});
            skArc(sketch, "E15.45.9", {"start": v(32.79, 0.98) * mm, "mid": v(32.75, 1.1) * mm, "end": v(32.66, 1.19) * mm});
            skArc(sketch, "E15.45.10", {"start": v(32.79, 0.98) * mm, "mid": v(32.8, 0.92) * mm, "end": v(32.8, 0.86) * mm});
            skArc(sketch, "E15.45.11", {"start": v(32.8, 0.74) * mm, "mid": v(32.8, 0.8) * mm, "end": v(32.8, 0.86) * mm});
            skArc(sketch, "E15.45.12", {"start": v(31.76, 1.64) * mm, "mid": v(31.7, 1.66) * mm, "end": v(31.65, 1.66) * mm});
            skArc(sketch, "E15.45.13", {"start": v(31.7, 0) * mm, "mid": v(31.75, 0) * mm, "end": v(31.8, 0.03) * mm});
            skArc(sketch, "E15.46.0", {"start": v(31.42, 4.95) * mm, "mid": v(31.9, 4.79) * mm, "end": v(32.36, 4.6) * mm});
            skLineSegment(sketch, "E15.46.1", {"start": v(31.52, 3.31) * mm, "end": v(30.52, 3.2) * mm});
            skLineSegment(sketch, "E15.46.2", {"start": v(31.3, 4.96) * mm, "end": v(30.3, 4.8) * mm});
            skPoint(sketch, "E15.46.3", {"position": v(32.56, 4.03) * mm});
            skPoint(sketch, "E15.46.4", {"position": v(31.58, 3.32) * mm});
            skArc(sketch, "E15.46.5", {"start": v(31.63, 3.35) * mm, "mid": v(32.05, 3.63) * mm, "end": v(32.45, 3.94) * mm});
            skPoint(sketch, "E15.46.6", {"position": v(32.49, 4.54) * mm});
            skPoint(sketch, "E15.46.7", {"position": v(31.36, 4.97) * mm});
            skArc(sketch, "E15.46.8", {"start": v(32.45, 3.94) * mm, "mid": v(32.52, 4.04) * mm, "end": v(32.54, 4.17) * mm});
            skArc(sketch, "E15.46.9", {"start": v(32.5, 4.4) * mm, "mid": v(32.46, 4.52) * mm, "end": v(32.36, 4.6) * mm});
            skArc(sketch, "E15.46.10", {"start": v(32.5, 4.4) * mm, "mid": v(32.52, 4.34) * mm, "end": v(32.52, 4.28) * mm});
            skArc(sketch, "E15.46.11", {"start": v(32.54, 4.17) * mm, "mid": v(32.53, 4.22) * mm, "end": v(32.52, 4.28) * mm});
            skArc(sketch, "E15.46.12", {"start": v(31.42, 4.95) * mm, "mid": v(31.36, 4.96) * mm, "end": v(31.3, 4.96) * mm});
            skArc(sketch, "E15.46.13", {"start": v(31.52, 3.31) * mm, "mid": v(31.57, 3.33) * mm, "end": v(31.63, 3.35) * mm});
            skArc(sketch, "E15.47.0", {"start": v(30.73, 8.2) * mm, "mid": v(31.22, 8.1) * mm, "end": v(31.7, 7.95) * mm});
            skLineSegment(sketch, "E15.47.1", {"start": v(31, 6.59) * mm, "end": v(30.01, 6.38) * mm});
            skLineSegment(sketch, "E15.47.2", {"start": v(30.61, 8.2) * mm, "end": v(29.64, 7.94) * mm});
            skPoint(sketch, "E15.47.3", {"position": v(31.96, 7.4) * mm});
            skPoint(sketch, "E15.47.4", {"position": v(31.06, 6.6) * mm});
            skArc(sketch, "E15.47.5", {"start": v(31.1, 6.64) * mm, "mid": v(31.5, 6.96) * mm, "end": v(31.86, 7.3) * mm});
            skPoint(sketch, "E15.47.6", {"position": v(31.84, 7.9) * mm});
            skPoint(sketch, "E15.47.7", {"position": v(30.67, 8.22) * mm});
            skArc(sketch, "E15.47.8", {"start": v(31.86, 7.3) * mm, "mid": v(31.92, 7.42) * mm, "end": v(31.92, 7.54) * mm});
            skArc(sketch, "E15.47.9", {"start": v(31.87, 7.77) * mm, "mid": v(31.8, 7.88) * mm, "end": v(31.7, 7.95) * mm});
            skArc(sketch, "E15.47.10", {"start": v(31.87, 7.77) * mm, "mid": v(31.88, 7.71) * mm, "end": v(31.9, 7.66) * mm});
            skArc(sketch, "E15.47.11", {"start": v(31.92, 7.54) * mm, "mid": v(31.91, 7.6) * mm, "end": v(31.9, 7.66) * mm});
            skArc(sketch, "E15.47.12", {"start": v(30.73, 8.2) * mm, "mid": v(30.67, 8.21) * mm, "end": v(30.61, 8.2) * mm});
            skArc(sketch, "E15.47.13", {"start": v(31, 6.59) * mm, "mid": v(31.05, 6.6) * mm, "end": v(31.1, 6.64) * mm});
            skArc(sketch, "E15.48.0", {"start": v(29.7, 11.37) * mm, "mid": v(30.2, 11.31) * mm, "end": v(30.7, 11.22) * mm});
            skLineSegment(sketch, "E15.48.1", {"start": v(30.14, 9.8) * mm, "end": v(29.18, 9.48) * mm});
            skLineSegment(sketch, "E15.48.2", {"start": v(29.59, 11.36) * mm, "end": v(28.65, 11) * mm});
            skPoint(sketch, "E15.48.3", {"position": v(31, 10.7) * mm});
            skPoint(sketch, "E15.48.4", {"position": v(30.2, 9.81) * mm});
            skArc(sketch, "E15.48.5", {"start": v(30.24, 9.85) * mm, "mid": v(30.6, 10.21) * mm, "end": v(30.92, 10.6) * mm});
            skPoint(sketch, "E15.48.6", {"position": v(30.84, 11.2) * mm});
            skPoint(sketch, "E15.48.7", {"position": v(29.64, 11.38) * mm});
            skArc(sketch, "E15.48.8", {"start": v(30.92, 10.6) * mm, "mid": v(30.97, 10.71) * mm, "end": v(30.96, 10.84) * mm});
            skArc(sketch, "E15.48.9", {"start": v(30.88, 11.06) * mm, "mid": v(30.81, 11.17) * mm, "end": v(30.7, 11.22) * mm});
            skArc(sketch, "E15.48.10", {"start": v(30.88, 11.06) * mm, "mid": v(30.9, 11) * mm, "end": v(30.92, 10.95) * mm});
            skArc(sketch, "E15.48.11", {"start": v(30.96, 10.84) * mm, "mid": v(30.94, 10.9) * mm, "end": v(30.92, 10.95) * mm});
            skArc(sketch, "E15.48.12", {"start": v(29.7, 11.37) * mm, "mid": v(29.64, 11.37) * mm, "end": v(29.59, 11.36) * mm});
            skArc(sketch, "E15.48.13", {"start": v(30.14, 9.8) * mm, "mid": v(30.2, 9.82) * mm, "end": v(30.24, 9.85) * mm});
            skArc(sketch, "E15.49.0", {"start": v(28.35, 14.42) * mm, "mid": v(28.85, 14.4) * mm, "end": v(29.36, 14.37) * mm});
            skLineSegment(sketch, "E15.49.1", {"start": v(28.95, 12.9) * mm, "end": v(28.03, 12.48) * mm});
            skLineSegment(sketch, "E15.49.2", {"start": v(28.24, 14.39) * mm, "end": v(27.34, 13.93) * mm});
            skPoint(sketch, "E15.49.3", {"position": v(29.72, 13.9) * mm});
            skPoint(sketch, "E15.49.4", {"position": v(29, 12.91) * mm});
            skArc(sketch, "E15.49.5", {"start": v(29.04, 12.96) * mm, "mid": v(29.36, 13.36) * mm, "end": v(29.64, 13.77) * mm});
            skPoint(sketch, "E15.49.6", {"position": v(29.5, 14.35) * mm});
            skPoint(sketch, "E15.49.7", {"position": v(28.29, 14.41) * mm});
            skArc(sketch, "E15.49.8", {"start": v(29.64, 13.77) * mm, "mid": v(29.68, 13.9) * mm, "end": v(29.66, 14.02) * mm});
            skArc(sketch, "E15.49.9", {"start": v(29.56, 14.23) * mm, "mid": v(29.48, 14.33) * mm, "end": v(29.36, 14.37) * mm});
            skArc(sketch, "E15.49.10", {"start": v(29.56, 14.23) * mm, "mid": v(29.58, 14.18) * mm, "end": v(29.6, 14.12) * mm});
            skArc(sketch, "E15.49.11", {"start": v(29.66, 14.02) * mm, "mid": v(29.63, 14.07) * mm, "end": v(29.6, 14.12) * mm});
            skArc(sketch, "E15.49.12", {"start": v(28.35, 14.42) * mm, "mid": v(28.3, 14.4) * mm, "end": v(28.24, 14.39) * mm});
            skArc(sketch, "E15.49.13", {"start": v(28.95, 12.9) * mm, "mid": v(29, 12.92) * mm, "end": v(29.04, 12.96) * mm});
            skArc(sketch, "E15.50.0", {"start": v(26.69, 17.3) * mm, "mid": v(27.19, 17.35) * mm, "end": v(27.7, 17.36) * mm});
            skLineSegment(sketch, "E15.50.1", {"start": v(27.45, 15.85) * mm, "end": v(26.57, 15.34) * mm});
            skLineSegment(sketch, "E15.50.2", {"start": v(26.58, 17.26) * mm, "end": v(25.73, 16.71) * mm});
            skPoint(sketch, "E15.50.3", {"position": v(28.1, 16.92) * mm});
            skPoint(sketch, "E15.50.4", {"position": v(27.5, 15.88) * mm});
            skArc(sketch, "E15.50.5", {"start": v(27.53, 15.92) * mm, "mid": v(27.8, 16.35) * mm, "end": v(28.04, 16.8) * mm});
            skPoint(sketch, "E15.50.6", {"position": v(27.84, 17.36) * mm});
            skPoint(sketch, "E15.50.7", {"position": v(26.63, 17.3) * mm});
            skArc(sketch, "E15.50.8", {"start": v(28.04, 16.8) * mm, "mid": v(28.07, 16.92) * mm, "end": v(28.03, 17.04) * mm});
            skArc(sketch, "E15.50.9", {"start": v(27.9, 17.24) * mm, "mid": v(27.82, 17.33) * mm, "end": v(27.7, 17.36) * mm});
            skArc(sketch, "E15.50.10", {"start": v(27.9, 17.24) * mm, "mid": v(27.94, 17.19) * mm, "end": v(27.97, 17.14) * mm});
            skArc(sketch, "E15.50.11", {"start": v(28.03, 17.04) * mm, "mid": v(28, 17.1) * mm, "end": v(27.97, 17.14) * mm});
            skArc(sketch, "E15.50.12", {"start": v(26.69, 17.3) * mm, "mid": v(26.63, 17.29) * mm, "end": v(26.58, 17.26) * mm});
            skArc(sketch, "E15.50.13", {"start": v(27.45, 15.85) * mm, "mid": v(27.5, 15.88) * mm, "end": v(27.53, 15.92) * mm});
            skArc(sketch, "E15.51.0", {"start": v(24.73, 20) * mm, "mid": v(25.23, 20.1) * mm, "end": v(25.73, 20.16) * mm});
            skLineSegment(sketch, "E15.51.1", {"start": v(25.64, 18.63) * mm, "end": v(24.82, 18.04) * mm});
            skLineSegment(sketch, "E15.51.2", {"start": v(24.63, 19.94) * mm, "end": v(23.85, 19.3) * mm});
            skPoint(sketch, "E15.51.3", {"position": v(26.18, 19.77) * mm});
            skPoint(sketch, "E15.51.4", {"position": v(25.69, 18.66) * mm});
            skArc(sketch, "E15.51.5", {"start": v(25.71, 18.71) * mm, "mid": v(25.94, 19.17) * mm, "end": v(26.13, 19.63) * mm});
            skPoint(sketch, "E15.51.6", {"position": v(25.87, 20.17) * mm});
            skPoint(sketch, "E15.51.7", {"position": v(24.67, 19.98) * mm});
            skArc(sketch, "E15.51.8", {"start": v(26.13, 19.63) * mm, "mid": v(26.15, 19.76) * mm, "end": v(26.1, 19.88) * mm});
            skArc(sketch, "E15.51.9", {"start": v(25.95, 20.06) * mm, "mid": v(25.85, 20.14) * mm, "end": v(25.73, 20.16) * mm});
            skArc(sketch, "E15.51.10", {"start": v(25.95, 20.06) * mm, "mid": v(25.99, 20.02) * mm, "end": v(26.03, 19.97) * mm});
            skArc(sketch, "E15.51.11", {"start": v(26.1, 19.88) * mm, "mid": v(26.06, 19.92) * mm, "end": v(26.03, 19.97) * mm});
            skArc(sketch, "E15.51.12", {"start": v(24.73, 20) * mm, "mid": v(24.68, 19.98) * mm, "end": v(24.63, 19.94) * mm});
            skArc(sketch, "E15.51.13", {"start": v(25.64, 18.63) * mm, "mid": v(25.68, 18.67) * mm, "end": v(25.71, 18.71) * mm});
            skArc(sketch, "E15.52.0", {"start": v(22.5, 22.47) * mm, "mid": v(22.99, 22.62) * mm, "end": v(23.48, 22.74) * mm});
            skLineSegment(sketch, "E15.52.1", {"start": v(23.55, 21.2) * mm, "end": v(22.8, 20.53) * mm});
            skLineSegment(sketch, "E15.52.2", {"start": v(22.4, 22.4) * mm, "end": v(21.7, 21.7) * mm});
            skPoint(sketch, "E15.52.3", {"position": v(23.97, 22.4) * mm});
            skPoint(sketch, "E15.52.4", {"position": v(23.6, 21.24) * mm});
            skArc(sketch, "E15.52.5", {"start": v(23.62, 21.3) * mm, "mid": v(23.8, 21.77) * mm, "end": v(23.94, 22.26) * mm});
            skPoint(sketch, "E15.52.6", {"position": v(23.62, 22.77) * mm});
            skPoint(sketch, "E15.52.7", {"position": v(22.45, 22.45) * mm});
            skArc(sketch, "E15.52.8", {"start": v(23.94, 22.26) * mm, "mid": v(23.94, 22.38) * mm, "end": v(23.88, 22.5) * mm});
            skArc(sketch, "E15.52.9", {"start": v(23.71, 22.67) * mm, "mid": v(23.6, 22.73) * mm, "end": v(23.48, 22.74) * mm});
            skArc(sketch, "E15.52.10", {"start": v(23.71, 22.67) * mm, "mid": v(23.75, 22.62) * mm, "end": v(23.8, 22.58) * mm});
            skArc(sketch, "E15.52.11", {"start": v(23.88, 22.5) * mm, "mid": v(23.84, 22.54) * mm, "end": v(23.8, 22.58) * mm});
            skArc(sketch, "E15.52.12", {"start": v(22.5, 22.47) * mm, "mid": v(22.45, 22.45) * mm, "end": v(22.4, 22.4) * mm});
            skArc(sketch, "E15.52.13", {"start": v(23.55, 21.2) * mm, "mid": v(23.59, 21.25) * mm, "end": v(23.62, 21.3) * mm});
            skArc(sketch, "E15.53.0", {"start": v(20.03, 24.7) * mm, "mid": v(20.5, 24.9) * mm, "end": v(20.97, 25.07) * mm});
            skLineSegment(sketch, "E15.53.1", {"start": v(21.2, 23.55) * mm, "end": v(20.53, 22.8) * mm});
            skLineSegment(sketch, "E15.53.2", {"start": v(19.94, 24.63) * mm, "end": v(19.3, 23.85) * mm});
            skPoint(sketch, "E15.53.3", {"position": v(21.5, 24.78) * mm});
            skPoint(sketch, "E15.53.4", {"position": v(21.24, 23.6) * mm});
            skArc(sketch, "E15.53.5", {"start": v(21.26, 23.65) * mm, "mid": v(21.39, 24.14) * mm, "end": v(21.48, 24.64) * mm});
            skPoint(sketch, "E15.53.6", {"position": v(21.1, 25.11) * mm});
            skPoint(sketch, "E15.53.7", {"position": v(19.98, 24.67) * mm});
            skArc(sketch, "E15.53.8", {"start": v(21.48, 24.64) * mm, "mid": v(21.47, 24.76) * mm, "end": v(21.4, 24.87) * mm});
            skArc(sketch, "E15.53.9", {"start": v(21.22, 25.02) * mm, "mid": v(21.1, 25.08) * mm, "end": v(20.97, 25.07) * mm});
            skArc(sketch, "E15.53.10", {"start": v(21.22, 25.02) * mm, "mid": v(21.26, 24.98) * mm, "end": v(21.3, 24.94) * mm});
            skArc(sketch, "E15.53.11", {"start": v(21.4, 24.87) * mm, "mid": v(21.35, 24.9) * mm, "end": v(21.3, 24.94) * mm});
            skArc(sketch, "E15.53.12", {"start": v(20.03, 24.7) * mm, "mid": v(19.99, 24.67) * mm, "end": v(19.94, 24.63) * mm});
            skArc(sketch, "E15.53.13", {"start": v(21.2, 23.55) * mm, "mid": v(21.24, 23.6) * mm, "end": v(21.26, 23.65) * mm});
            skArc(sketch, "E15.54.0", {"start": v(17.34, 26.66) * mm, "mid": v(17.78, 26.9) * mm, "end": v(18.24, 27.12) * mm});
            skLineSegment(sketch, "E15.54.1", {"start": v(18.63, 25.64) * mm, "end": v(18.04, 24.82) * mm});
            skLineSegment(sketch, "E15.54.2", {"start": v(17.26, 26.58) * mm, "end": v(16.71, 25.73) * mm});
            skPoint(sketch, "E15.54.3", {"position": v(18.8, 26.89) * mm});
            skPoint(sketch, "E15.54.4", {"position": v(18.66, 25.69) * mm});
            skArc(sketch, "E15.54.5", {"start": v(18.67, 25.74) * mm, "mid": v(18.75, 26.24) * mm, "end": v(18.79, 26.75) * mm});
            skPoint(sketch, "E15.54.6", {"position": v(18.37, 27.18) * mm});
            skPoint(sketch, "E15.54.7", {"position": v(17.3, 26.63) * mm});
            skArc(sketch, "E15.54.8", {"start": v(18.79, 26.75) * mm, "mid": v(18.76, 26.87) * mm, "end": v(18.68, 26.97) * mm});
            skArc(sketch, "E15.54.9", {"start": v(18.48, 27.1) * mm, "mid": v(18.36, 27.14) * mm, "end": v(18.24, 27.12) * mm});
            skArc(sketch, "E15.54.10", {"start": v(18.48, 27.1) * mm, "mid": v(18.53, 27.07) * mm, "end": v(18.58, 27.03) * mm});
            skArc(sketch, "E15.54.11", {"start": v(18.68, 26.97) * mm, "mid": v(18.63, 27) * mm, "end": v(18.58, 27.03) * mm});
            skArc(sketch, "E15.54.12", {"start": v(17.34, 26.66) * mm, "mid": v(17.3, 26.62) * mm, "end": v(17.26, 26.58) * mm});
            skArc(sketch, "E15.54.13", {"start": v(18.63, 25.64) * mm, "mid": v(18.66, 25.69) * mm, "end": v(18.67, 25.74) * mm});
            skArc(sketch, "E15.55.0", {"start": v(14.46, 28.33) * mm, "mid": v(14.87, 28.62) * mm, "end": v(15.3, 28.88) * mm});
            skLineSegment(sketch, "E15.55.1", {"start": v(15.85, 27.45) * mm, "end": v(15.34, 26.57) * mm});
            skLineSegment(sketch, "E15.55.2", {"start": v(14.39, 28.24) * mm, "end": v(13.93, 27.34) * mm});
            skPoint(sketch, "E15.55.3", {"position": v(15.88, 28.7) * mm});
            skPoint(sketch, "E15.55.4", {"position": v(15.87, 27.5) * mm});
            skArc(sketch, "E15.55.5", {"start": v(15.88, 27.56) * mm, "mid": v(15.9, 28.06) * mm, "end": v(15.89, 28.56) * mm});
            skPoint(sketch, "E15.55.6", {"position": v(15.43, 28.95) * mm});
            skPoint(sketch, "E15.55.7", {"position": v(14.41, 28.29) * mm});
            skArc(sketch, "E15.55.8", {"start": v(15.89, 28.56) * mm, "mid": v(15.85, 28.69) * mm, "end": v(15.76, 28.77) * mm});
            skArc(sketch, "E15.55.9", {"start": v(15.55, 28.88) * mm, "mid": v(15.43, 28.91) * mm, "end": v(15.3, 28.88) * mm});
            skArc(sketch, "E15.55.10", {"start": v(15.55, 28.88) * mm, "mid": v(15.6, 28.86) * mm, "end": v(15.65, 28.83) * mm});
            skArc(sketch, "E15.55.11", {"start": v(15.76, 28.77) * mm, "mid": v(15.7, 28.8) * mm, "end": v(15.65, 28.83) * mm});
            skArc(sketch, "E15.55.12", {"start": v(14.46, 28.33) * mm, "mid": v(14.42, 28.29) * mm, "end": v(14.39, 28.24) * mm});
            skArc(sketch, "E15.55.13", {"start": v(15.85, 27.45) * mm, "mid": v(15.87, 27.5) * mm, "end": v(15.88, 27.56) * mm});
            skArc(sketch, "E15.56.0", {"start": v(11.42, 29.68) * mm, "mid": v(11.8, 30.01) * mm, "end": v(12.2, 30.32) * mm});
            skLineSegment(sketch, "E15.56.1", {"start": v(12.9, 28.95) * mm, "end": v(12.48, 28.03) * mm});
            skLineSegment(sketch, "E15.56.2", {"start": v(11.36, 29.59) * mm, "end": v(11, 28.65) * mm});
            skPoint(sketch, "E15.56.3", {"position": v(12.8, 30.2) * mm});
            skPoint(sketch, "E15.56.4", {"position": v(12.91, 29) * mm});
            skArc(sketch, "E15.56.5", {"start": v(12.91, 29.06) * mm, "mid": v(12.88, 29.57) * mm, "end": v(12.81, 30.07) * mm});
            skPoint(sketch, "E15.56.6", {"position": v(12.32, 30.4) * mm});
            skPoint(sketch, "E15.56.7", {"position": v(11.38, 29.64) * mm});
            skArc(sketch, "E15.56.8", {"start": v(12.81, 30.07) * mm, "mid": v(12.76, 30.18) * mm, "end": v(12.66, 30.26) * mm});
            skArc(sketch, "E15.56.9", {"start": v(12.45, 30.35) * mm, "mid": v(12.32, 30.37) * mm, "end": v(12.2, 30.32) * mm});
            skArc(sketch, "E15.56.10", {"start": v(12.45, 30.35) * mm, "mid": v(12.5, 30.33) * mm, "end": v(12.55, 30.3) * mm});
            skArc(sketch, "E15.56.11", {"start": v(12.66, 30.26) * mm, "mid": v(12.6, 30.28) * mm, "end": v(12.55, 30.3) * mm});
            skArc(sketch, "E15.56.12", {"start": v(11.42, 29.68) * mm, "mid": v(11.38, 29.64) * mm, "end": v(11.36, 29.59) * mm});
            skArc(sketch, "E15.56.13", {"start": v(12.9, 28.95) * mm, "mid": v(12.9, 29) * mm, "end": v(12.91, 29.06) * mm});
            skArc(sketch, "E15.57.0", {"start": v(8.26, 30.71) * mm, "mid": v(8.6, 31.08) * mm, "end": v(8.96, 31.43) * mm});
            skLineSegment(sketch, "E15.57.1", {"start": v(9.8, 30.14) * mm, "end": v(9.48, 29.18) * mm});
            skLineSegment(sketch, "E15.57.2", {"start": v(8.2, 30.61) * mm, "end": v(7.94, 29.64) * mm});
            skPoint(sketch, "E15.57.3", {"position": v(9.56, 31.38) * mm});
            skPoint(sketch, "E15.57.4", {"position": v(9.81, 30.2) * mm});
            skArc(sketch, "E15.57.5", {"start": v(9.8, 30.25) * mm, "mid": v(9.72, 30.75) * mm, "end": v(9.6, 31.24) * mm});
            skPoint(sketch, "E15.57.6", {"position": v(9.07, 31.53) * mm});
            skPoint(sketch, "E15.57.7", {"position": v(8.22, 30.67) * mm});
            skArc(sketch, "E15.57.8", {"start": v(9.6, 31.24) * mm, "mid": v(9.54, 31.35) * mm, "end": v(9.43, 31.42) * mm});
            skArc(sketch, "E15.57.9", {"start": v(9.2, 31.49) * mm, "mid": v(9.08, 31.5) * mm, "end": v(8.96, 31.43) * mm});
            skArc(sketch, "E15.57.10", {"start": v(9.2, 31.49) * mm, "mid": v(9.26, 31.47) * mm, "end": v(9.32, 31.45) * mm});
            skArc(sketch, "E15.57.11", {"start": v(9.43, 31.42) * mm, "mid": v(9.37, 31.44) * mm, "end": v(9.32, 31.45) * mm});
            skArc(sketch, "E15.57.12", {"start": v(8.26, 30.71) * mm, "mid": v(8.22, 30.67) * mm, "end": v(8.2, 30.61) * mm});
            skArc(sketch, "E15.57.13", {"start": v(9.8, 30.14) * mm, "mid": v(9.8, 30.2) * mm, "end": v(9.8, 30.25) * mm});
            skArc(sketch, "E15.58.0", {"start": v(5, 31.4) * mm, "mid": v(5.3, 31.81) * mm, "end": v(5.63, 32.2) * mm});
            skLineSegment(sketch, "E15.58.1", {"start": v(6.59, 31) * mm, "end": v(6.38, 30.01) * mm});
            skLineSegment(sketch, "E15.58.2", {"start": v(4.96, 31.3) * mm, "end": v(4.8, 30.3) * mm});
            skPoint(sketch, "E15.58.3", {"position": v(6.23, 32.2) * mm});
            skPoint(sketch, "E15.58.4", {"position": v(6.6, 31.06) * mm});
            skArc(sketch, "E15.58.5", {"start": v(6.59, 31.11) * mm, "mid": v(6.45, 31.6) * mm, "end": v(6.28, 32.08) * mm});
            skPoint(sketch, "E15.58.6", {"position": v(5.73, 32.3) * mm});
            skPoint(sketch, "E15.58.7", {"position": v(4.97, 31.36) * mm});
            skArc(sketch, "E15.58.8", {"start": v(6.28, 32.08) * mm, "mid": v(6.2, 32.18) * mm, "end": v(6.1, 32.23) * mm});
            skArc(sketch, "E15.58.9", {"start": v(5.86, 32.28) * mm, "mid": v(5.74, 32.27) * mm, "end": v(5.63, 32.2) * mm});
            skArc(sketch, "E15.58.10", {"start": v(5.86, 32.28) * mm, "mid": v(5.92, 32.27) * mm, "end": v(5.98, 32.25) * mm});
            skArc(sketch, "E15.58.11", {"start": v(6.1, 32.23) * mm, "mid": v(6.04, 32.24) * mm, "end": v(5.98, 32.25) * mm});
            skArc(sketch, "E15.58.12", {"start": v(5, 31.4) * mm, "mid": v(4.97, 31.36) * mm, "end": v(4.96, 31.3) * mm});
            skArc(sketch, "E15.58.13", {"start": v(6.59, 31) * mm, "mid": v(6.6, 31.06) * mm, "end": v(6.59, 31.11) * mm});
            skArc(sketch, "E15.59.0", {"start": v(1.69, 31.76) * mm, "mid": v(1.95, 32.2) * mm, "end": v(2.23, 32.6) * mm});
            skLineSegment(sketch, "E15.59.1", {"start": v(3.31, 31.52) * mm, "end": v(3.2, 30.52) * mm});
            skLineSegment(sketch, "E15.59.2", {"start": v(1.66, 31.65) * mm, "end": v(1.6, 30.64) * mm});
            skPoint(sketch, "E15.59.3", {"position": v(2.83, 32.68) * mm});
            skPoint(sketch, "E15.59.4", {"position": v(3.32, 31.58) * mm});
            skArc(sketch, "E15.59.5", {"start": v(3.3, 31.63) * mm, "mid": v(3.11, 32.1) * mm, "end": v(2.9, 32.56) * mm});
            skPoint(sketch, "E15.59.6", {"position": v(2.32, 32.72) * mm});
            skPoint(sketch, "E15.59.7", {"position": v(1.66, 31.7) * mm});
            skArc(sketch, "E15.59.8", {"start": v(2.9, 32.56) * mm, "mid": v(2.81, 32.65) * mm, "end": v(2.7, 32.7) * mm});
            skArc(sketch, "E15.59.9", {"start": v(2.46, 32.71) * mm, "mid": v(2.33, 32.69) * mm, "end": v(2.23, 32.6) * mm});
            skArc(sketch, "E15.59.10", {"start": v(2.46, 32.71) * mm, "mid": v(2.52, 32.7) * mm, "end": v(2.57, 32.7) * mm});
            skArc(sketch, "E15.59.11", {"start": v(2.7, 32.7) * mm, "mid": v(2.63, 32.7) * mm, "end": v(2.57, 32.7) * mm});
            skArc(sketch, "E15.59.12", {"start": v(1.69, 31.76) * mm, "mid": v(1.67, 31.7) * mm, "end": v(1.66, 31.65) * mm});
            skArc(sketch, "E15.59.13", {"start": v(3.31, 31.52) * mm, "mid": v(3.31, 31.58) * mm, "end": v(3.3, 31.63) * mm});
            skSolve(sketch);
        }
        {
            var Q0;
            Q0 = qSketchRegion(id + "F0", true);
            var Q1;
            {var subQ0=sQuery(id+"F0.wireOp",EDGE,"E0");var subQ27=makeQuery(id+"F0.imprint","INTERSECT",VERTEX,{"derivedFrom":[subQ0,sQuery(id+"F0.wireOp",EDGE,"E15.45.1")]});Q1=makeQuery(id+"F0.imprint","IMPRINT",FACE,{"disambiguationData":[TD([[makeQuery(id+"F0.imprint","IMPRINT",EDGE,{"disambiguationData":[TD([[subQ27,-1.0]])],"derivedFrom":subQ0}),1.0]])]});}
            extrude(context, id + "F1", {"entities" : qUnion([Q0, Q1]), "depth" : 6.35 * mm});
        }
        {
            var Q0;
            Q0=qCreatedBy(makeId("Front.planeOp"),FACE);
            var sketch = newSketch(context, id + "F2", { "sketchPlane" : qUnion([Q0])});
            skCircle(sketch, "E16", {"center": v(0, 0) * mm, "radius": 5.59 * mm});
            skSolve(sketch);
        }
        {
            var Q0;
            Q0=makeQuery(id+"F2.imprint","IMPRINT",FACE,{"disambiguationData":[TD([[makeQuery(id+"F2.imprint","IMPRINT",EDGE,{"derivedFrom":sQuery(id+"F2.wireOp",EDGE,"E16")}),1.0]])]});
            extrude(context, id + "F3", {"entities" : qUnion([Q0]), "operationType" : NewBodyOperationType.REMOVE, "depth" : 12.7 * mm});
        }
    });
